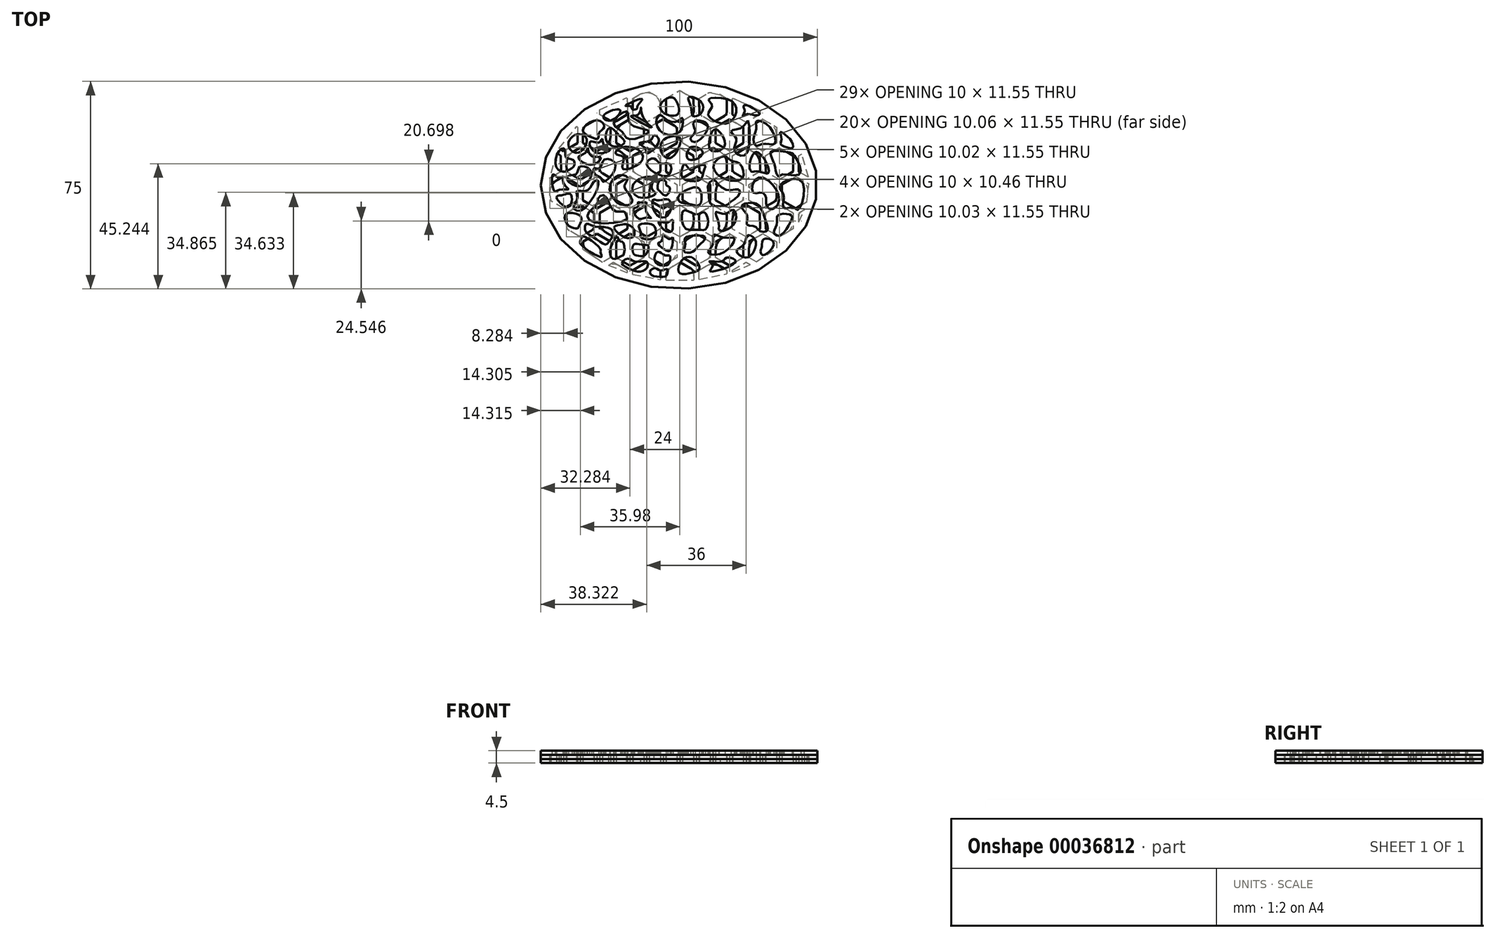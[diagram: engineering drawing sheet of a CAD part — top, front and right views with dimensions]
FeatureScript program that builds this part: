
annotation { "Feature Type Name" : "Feature", "Feature Type Description" : "" }
export const myFeature = defineFeature(function(context is Context, id is Id, definition is map)
    precondition{}
    {
        {
            var Q0;
            Q0=qCreatedBy(makeId("Top.planeOp"),FACE);
            var sketch = newSketch(context, id + "F0", { "sketchPlane" : qUnion([Q0])});
            skEllipse(sketch, "E0", {"center": v(0, 0) * mm, "majorRadius": 37.5 * mm, "minorRadius": 50 * mm, "majorAxis": v(0, 1)});
            skCircle(sketch, "E1.cCircle", {"center": v(-71.7, 28.44) * mm, "radius": 5 * mm, "construction": true});
            skLineSegment(sketch, "E1.0", {"start": v(-66.66, 25.61) * mm, "end": v(-71.63, 22.67) * mm, "construction": true});
            skLineSegment(sketch, "E1.1", {"start": v(-71.63, 22.67) * mm, "end": v(-76.66, 25.5) * mm, "construction": true});
            skLineSegment(sketch, "E1.2", {"start": v(-76.66, 25.5) * mm, "end": v(-76.73, 31.27) * mm, "construction": true});
            skLineSegment(sketch, "E1.3", {"start": v(-76.73, 31.27) * mm, "end": v(-71.76, 34.22) * mm, "construction": true});
            skLineSegment(sketch, "E1.4", {"start": v(-71.76, 34.22) * mm, "end": v(-66.73, 31.39) * mm, "construction": true});
            skLineSegment(sketch, "E1.5", {"start": v(-66.73, 31.39) * mm, "end": v(-66.66, 25.61) * mm, "construction": true});
            skPoint(sketch, "E1.0.midPoint", {"position": v(-69.15, 24.14) * mm});
            skPoint(sketch, "E2", {"position": v(-77.72, 18.06) * mm});
            skLineSegment(sketch, "E3", {"start": v(-71.7, 28.44) * mm, "end": v(-74.15, 24.08) * mm, "construction": true});
            skLineSegment(sketch, "E4", {"start": v(-71.7, 28.44) * mm, "end": v(-71.63, 14.25) * mm, "construction": true});
            skCircle(sketch, "E5.cCircle", {"center": v(-77.72, 18.06) * mm, "radius": 5 * mm, "construction": true});
            skLineSegment(sketch, "E5.0", {"start": v(-77.72, 23.84) * mm, "end": v(-72.72, 20.95) * mm, "construction": true});
            skLineSegment(sketch, "E5.1", {"start": v(-72.72, 20.95) * mm, "end": v(-72.72, 15.18) * mm, "construction": true});
            skLineSegment(sketch, "E5.2", {"start": v(-72.72, 15.18) * mm, "end": v(-77.72, 12.29) * mm, "construction": true});
            skLineSegment(sketch, "E5.3", {"start": v(-77.72, 12.29) * mm, "end": v(-82.72, 15.18) * mm, "construction": true});
            skLineSegment(sketch, "E5.4", {"start": v(-82.72, 15.18) * mm, "end": v(-82.72, 20.95) * mm, "construction": true});
            skLineSegment(sketch, "E5.5", {"start": v(-82.72, 20.95) * mm, "end": v(-77.72, 23.84) * mm, "construction": true});
            skPoint(sketch, "E5.0.midPoint", {"position": v(-75.22, 22.4) * mm});
            skLineSegment(sketch, "E6.0.1.0", {"start": v(-76.73, 10.57) * mm, "end": v(-71.76, 13.52) * mm});
            skLineSegment(sketch, "E6.0.1.1", {"start": v(-71.76, 13.52) * mm, "end": v(-66.73, 10.69) * mm});
            skLineSegment(sketch, "E6.0.1.2", {"start": v(-66.73, 10.69) * mm, "end": v(-66.66, 4.91) * mm});
            skLineSegment(sketch, "E6.0.1.3", {"start": v(-66.66, 4.91) * mm, "end": v(-71.63, 1.97) * mm});
            skLineSegment(sketch, "E6.0.1.4", {"start": v(-71.63, 1.97) * mm, "end": v(-76.66, 4.8) * mm});
            skLineSegment(sketch, "E6.0.1.5", {"start": v(-76.66, 4.8) * mm, "end": v(-76.73, 10.57) * mm});
            skLineSegment(sketch, "E6.0.1.6", {"start": v(-82.72, 0.25) * mm, "end": v(-77.72, 3.14) * mm});
            skLineSegment(sketch, "E6.0.1.7", {"start": v(-77.72, 3.14) * mm, "end": v(-72.72, 0.25) * mm});
            skLineSegment(sketch, "E6.0.1.8", {"start": v(-72.72, 0.25) * mm, "end": v(-72.72, -5.52) * mm});
            skLineSegment(sketch, "E6.0.1.9", {"start": v(-72.72, -5.52) * mm, "end": v(-77.72, -8.4) * mm});
            skLineSegment(sketch, "E6.0.1.10", {"start": v(-77.72, -8.4) * mm, "end": v(-82.72, -5.52) * mm});
            skLineSegment(sketch, "E6.0.1.11", {"start": v(-82.72, -5.52) * mm, "end": v(-82.72, 0.25) * mm});
            skLineSegment(sketch, "E6.0.2.0", {"start": v(-76.73, -10.12) * mm, "end": v(-71.76, -7.18) * mm});
            skLineSegment(sketch, "E6.0.2.1", {"start": v(-71.76, -7.18) * mm, "end": v(-66.73, -10.01) * mm});
            skLineSegment(sketch, "E6.0.2.2", {"start": v(-66.73, -10.01) * mm, "end": v(-66.66, -15.78) * mm});
            skLineSegment(sketch, "E6.0.2.3", {"start": v(-66.66, -15.78) * mm, "end": v(-71.63, -18.73) * mm});
            skLineSegment(sketch, "E6.0.2.4", {"start": v(-71.63, -18.73) * mm, "end": v(-76.66, -15.9) * mm});
            skLineSegment(sketch, "E6.0.2.5", {"start": v(-76.66, -15.9) * mm, "end": v(-76.73, -10.12) * mm});
            skLineSegment(sketch, "E6.0.2.6", {"start": v(-82.72, -20.45) * mm, "end": v(-77.72, -17.56) * mm});
            skLineSegment(sketch, "E6.0.2.7", {"start": v(-77.72, -17.56) * mm, "end": v(-72.72, -20.45) * mm});
            skLineSegment(sketch, "E6.0.2.8", {"start": v(-72.72, -20.45) * mm, "end": v(-72.72, -26.22) * mm});
            skLineSegment(sketch, "E6.0.2.9", {"start": v(-72.72, -26.22) * mm, "end": v(-77.72, -29.1) * mm});
            skLineSegment(sketch, "E6.0.2.10", {"start": v(-77.72, -29.1) * mm, "end": v(-82.72, -26.22) * mm});
            skLineSegment(sketch, "E6.0.2.11", {"start": v(-82.72, -26.22) * mm, "end": v(-82.72, -20.45) * mm});
            skLineSegment(sketch, "E6.0.3.0", {"start": v(-76.73, -30.82) * mm, "end": v(-71.76, -27.88) * mm});
            skLineSegment(sketch, "E6.0.3.1", {"start": v(-71.76, -27.88) * mm, "end": v(-66.73, -30.7) * mm});
            skLineSegment(sketch, "E6.0.3.2", {"start": v(-66.73, -30.7) * mm, "end": v(-66.66, -36.48) * mm});
            skLineSegment(sketch, "E6.0.3.3", {"start": v(-66.66, -36.48) * mm, "end": v(-71.63, -39.42) * mm});
            skLineSegment(sketch, "E6.0.3.4", {"start": v(-71.63, -39.42) * mm, "end": v(-76.66, -36.6) * mm});
            skLineSegment(sketch, "E6.0.3.5", {"start": v(-76.66, -36.6) * mm, "end": v(-76.73, -30.82) * mm});
            skLineSegment(sketch, "E6.0.3.6", {"start": v(-82.72, -41.14) * mm, "end": v(-77.72, -38.26) * mm});
            skLineSegment(sketch, "E6.0.3.7", {"start": v(-77.72, -38.26) * mm, "end": v(-72.72, -41.14) * mm});
            skLineSegment(sketch, "E6.0.3.8", {"start": v(-72.72, -41.14) * mm, "end": v(-72.72, -46.92) * mm});
            skLineSegment(sketch, "E6.0.3.9", {"start": v(-72.72, -46.92) * mm, "end": v(-77.72, -49.8) * mm});
            skLineSegment(sketch, "E6.0.3.10", {"start": v(-77.72, -49.8) * mm, "end": v(-82.72, -46.92) * mm});
            skLineSegment(sketch, "E6.0.3.11", {"start": v(-82.72, -46.92) * mm, "end": v(-82.72, -41.14) * mm});
            skLineSegment(sketch, "E6.1.1.0", {"start": v(-64.73, 10.57) * mm, "end": v(-59.76, 13.52) * mm});
            skLineSegment(sketch, "E6.1.1.1", {"start": v(-59.76, 13.52) * mm, "end": v(-54.73, 10.69) * mm});
            skLineSegment(sketch, "E6.1.1.2", {"start": v(-54.73, 10.69) * mm, "end": v(-54.66, 4.91) * mm});
            skLineSegment(sketch, "E6.1.1.3", {"start": v(-54.66, 4.91) * mm, "end": v(-59.63, 1.97) * mm});
            skLineSegment(sketch, "E6.1.1.4", {"start": v(-59.63, 1.97) * mm, "end": v(-64.66, 4.8) * mm});
            skLineSegment(sketch, "E6.1.1.5", {"start": v(-64.66, 4.8) * mm, "end": v(-64.73, 10.57) * mm});
            skLineSegment(sketch, "E6.1.1.6", {"start": v(-70.72, 0.25) * mm, "end": v(-65.72, 3.14) * mm});
            skLineSegment(sketch, "E6.1.1.7", {"start": v(-65.72, 3.14) * mm, "end": v(-60.72, 0.25) * mm});
            skLineSegment(sketch, "E6.1.1.8", {"start": v(-60.72, 0.25) * mm, "end": v(-60.72, -5.52) * mm});
            skLineSegment(sketch, "E6.1.1.9", {"start": v(-60.72, -5.52) * mm, "end": v(-65.72, -8.4) * mm});
            skLineSegment(sketch, "E6.1.1.10", {"start": v(-65.72, -8.4) * mm, "end": v(-70.72, -5.52) * mm});
            skLineSegment(sketch, "E6.1.1.11", {"start": v(-70.72, -5.52) * mm, "end": v(-70.72, 0.25) * mm});
            skLineSegment(sketch, "E6.1.2.0", {"start": v(-64.73, -10.12) * mm, "end": v(-59.76, -7.18) * mm});
            skLineSegment(sketch, "E6.1.2.1", {"start": v(-59.76, -7.18) * mm, "end": v(-54.73, -10.01) * mm});
            skLineSegment(sketch, "E6.1.2.2", {"start": v(-54.73, -10.01) * mm, "end": v(-54.66, -15.78) * mm});
            skLineSegment(sketch, "E6.1.2.3", {"start": v(-54.66, -15.78) * mm, "end": v(-59.63, -18.73) * mm});
            skLineSegment(sketch, "E6.1.2.4", {"start": v(-59.63, -18.73) * mm, "end": v(-64.66, -15.9) * mm});
            skLineSegment(sketch, "E6.1.2.5", {"start": v(-64.66, -15.9) * mm, "end": v(-64.73, -10.12) * mm});
            skLineSegment(sketch, "E6.1.2.6", {"start": v(-70.72, -20.45) * mm, "end": v(-65.72, -17.56) * mm});
            skLineSegment(sketch, "E6.1.2.7", {"start": v(-65.72, -17.56) * mm, "end": v(-60.72, -20.45) * mm});
            skLineSegment(sketch, "E6.1.2.8", {"start": v(-60.72, -20.45) * mm, "end": v(-60.72, -26.22) * mm});
            skLineSegment(sketch, "E6.1.2.9", {"start": v(-60.72, -26.22) * mm, "end": v(-65.72, -29.1) * mm});
            skLineSegment(sketch, "E6.1.2.10", {"start": v(-65.72, -29.1) * mm, "end": v(-70.72, -26.22) * mm});
            skLineSegment(sketch, "E6.1.2.11", {"start": v(-70.72, -26.22) * mm, "end": v(-70.72, -20.45) * mm});
            skLineSegment(sketch, "E6.1.3.0", {"start": v(-64.73, -30.82) * mm, "end": v(-59.76, -27.88) * mm});
            skLineSegment(sketch, "E6.1.3.1", {"start": v(-59.76, -27.88) * mm, "end": v(-54.73, -30.7) * mm});
            skLineSegment(sketch, "E6.1.3.2", {"start": v(-54.73, -30.7) * mm, "end": v(-54.66, -36.48) * mm});
            skLineSegment(sketch, "E6.1.3.3", {"start": v(-54.66, -36.48) * mm, "end": v(-59.63, -39.42) * mm});
            skLineSegment(sketch, "E6.1.3.4", {"start": v(-59.63, -39.42) * mm, "end": v(-64.66, -36.6) * mm});
            skLineSegment(sketch, "E6.1.3.5", {"start": v(-64.66, -36.6) * mm, "end": v(-64.73, -30.82) * mm});
            skLineSegment(sketch, "E6.1.3.6", {"start": v(-70.72, -41.14) * mm, "end": v(-65.72, -38.26) * mm});
            skLineSegment(sketch, "E6.1.3.7", {"start": v(-65.72, -38.26) * mm, "end": v(-60.72, -41.14) * mm});
            skLineSegment(sketch, "E6.1.3.8", {"start": v(-60.72, -41.14) * mm, "end": v(-60.72, -46.92) * mm});
            skLineSegment(sketch, "E6.1.3.9", {"start": v(-60.72, -46.92) * mm, "end": v(-65.72, -49.8) * mm});
            skLineSegment(sketch, "E6.1.3.10", {"start": v(-65.72, -49.8) * mm, "end": v(-70.72, -46.92) * mm});
            skLineSegment(sketch, "E6.1.3.11", {"start": v(-70.72, -46.92) * mm, "end": v(-70.72, -41.14) * mm});
            skLineSegment(sketch, "E6.2.1.2", {"start": v(-42.73, 10.69) * mm, "end": v(-42.66, 4.91) * mm});
            skLineSegment(sketch, "E6.2.1.3", {"start": v(-42.66, 4.91) * mm, "end": v(-46.88, 2.41) * mm});
            skLineSegment(sketch, "E6.2.2.6", {"start": v(-58.72, -20.45) * mm, "end": v(-53.72, -17.56) * mm});
            skLineSegment(sketch, "E6.2.2.7", {"start": v(-53.72, -17.56) * mm, "end": v(-48.72, -20.45) * mm});
            skLineSegment(sketch, "E6.2.2.8", {"start": v(-48.72, -20.45) * mm, "end": v(-48.72, -26.22) * mm});
            skLineSegment(sketch, "E6.2.2.9", {"start": v(-48.72, -26.22) * mm, "end": v(-53.72, -29.1) * mm});
            skLineSegment(sketch, "E6.2.2.10", {"start": v(-53.72, -29.1) * mm, "end": v(-58.72, -26.22) * mm});
            skLineSegment(sketch, "E6.2.2.11", {"start": v(-58.72, -26.22) * mm, "end": v(-58.72, -20.45) * mm});
            skLineSegment(sketch, "E6.2.3.0", {"start": v(-52.73, -30.82) * mm, "end": v(-47.76, -27.88) * mm});
            skLineSegment(sketch, "E6.2.3.1", {"start": v(-47.76, -27.88) * mm, "end": v(-42.73, -30.7) * mm});
            skLineSegment(sketch, "E6.2.3.2", {"start": v(-42.73, -30.7) * mm, "end": v(-42.66, -36.48) * mm});
            skLineSegment(sketch, "E6.2.3.3", {"start": v(-42.66, -36.48) * mm, "end": v(-47.63, -39.42) * mm});
            skLineSegment(sketch, "E6.2.3.4", {"start": v(-47.63, -39.42) * mm, "end": v(-52.66, -36.6) * mm});
            skLineSegment(sketch, "E6.2.3.5", {"start": v(-52.66, -36.6) * mm, "end": v(-52.73, -30.82) * mm});
            skLineSegment(sketch, "E6.2.3.6", {"start": v(-58.72, -41.14) * mm, "end": v(-53.72, -38.26) * mm});
            skLineSegment(sketch, "E6.2.3.7", {"start": v(-53.72, -38.26) * mm, "end": v(-48.72, -41.14) * mm});
            skLineSegment(sketch, "E6.2.3.8", {"start": v(-48.72, -41.14) * mm, "end": v(-48.72, -46.92) * mm});
            skLineSegment(sketch, "E6.2.3.9", {"start": v(-48.72, -46.92) * mm, "end": v(-53.72, -49.8) * mm});
            skLineSegment(sketch, "E6.2.3.10", {"start": v(-53.72, -49.8) * mm, "end": v(-58.72, -46.92) * mm});
            skLineSegment(sketch, "E6.2.3.11", {"start": v(-58.72, -46.92) * mm, "end": v(-58.72, -41.14) * mm});
            skLineSegment(sketch, "E6.3.0.8", {"start": v(-36.72, 20.95) * mm, "end": v(-36.72, 15.18) * mm});
            skLineSegment(sketch, "E6.3.0.9", {"start": v(-36.72, 15.18) * mm, "end": v(-41.72, 12.29) * mm});
            skLineSegment(sketch, "E6.3.0.10", {"start": v(-41.72, 12.29) * mm, "end": v(-43.37, 13.25) * mm});
            skLineSegment(sketch, "E6.3.1.0", {"start": v(-40.73, 10.57) * mm, "end": v(-35.76, 13.52) * mm});
            skLineSegment(sketch, "E6.3.1.1", {"start": v(-35.76, 13.52) * mm, "end": v(-30.73, 10.69) * mm});
            skLineSegment(sketch, "E6.3.1.2", {"start": v(-30.73, 10.69) * mm, "end": v(-30.66, 4.91) * mm});
            skLineSegment(sketch, "E6.3.1.3", {"start": v(-30.66, 4.91) * mm, "end": v(-35.63, 1.97) * mm});
            skLineSegment(sketch, "E6.3.1.4", {"start": v(-35.63, 1.97) * mm, "end": v(-40.66, 4.8) * mm});
            skLineSegment(sketch, "E6.3.1.5", {"start": v(-40.66, 4.8) * mm, "end": v(-40.73, 10.57) * mm});
            skLineSegment(sketch, "E6.3.1.6", {"start": v(-46.72, 0.25) * mm, "end": v(-41.72, 3.14) * mm});
            skLineSegment(sketch, "E6.3.1.7", {"start": v(-41.72, 3.14) * mm, "end": v(-36.72, 0.25) * mm});
            skLineSegment(sketch, "E6.3.1.8", {"start": v(-36.72, 0.25) * mm, "end": v(-36.72, -5.52) * mm});
            skLineSegment(sketch, "E6.3.1.9", {"start": v(-36.72, -5.52) * mm, "end": v(-41.72, -8.4) * mm});
            skLineSegment(sketch, "E6.3.1.10", {"start": v(-41.72, -8.4) * mm, "end": v(-46.34, -5.74) * mm});
            skLineSegment(sketch, "E6.3.1.11", {"start": v(-46.72, -3.77) * mm, "end": v(-46.72, 0.25) * mm});
            skLineSegment(sketch, "E6.3.2.0", {"start": v(-40.73, -10.12) * mm, "end": v(-35.76, -7.18) * mm});
            skLineSegment(sketch, "E6.3.2.1", {"start": v(-35.76, -7.18) * mm, "end": v(-30.73, -10.01) * mm});
            skLineSegment(sketch, "E6.3.2.2", {"start": v(-30.73, -10.01) * mm, "end": v(-30.66, -15.78) * mm});
            skLineSegment(sketch, "E6.3.2.3", {"start": v(-30.66, -15.78) * mm, "end": v(-35.63, -18.73) * mm});
            skLineSegment(sketch, "E6.3.2.4", {"start": v(-35.63, -18.73) * mm, "end": v(-40.66, -15.9) * mm});
            skLineSegment(sketch, "E6.3.2.5", {"start": v(-40.66, -15.9) * mm, "end": v(-40.73, -10.12) * mm});
            skLineSegment(sketch, "E6.3.3.0", {"start": v(-40.73, -30.82) * mm, "end": v(-35.76, -27.88) * mm});
            skLineSegment(sketch, "E6.3.3.1", {"start": v(-35.76, -27.88) * mm, "end": v(-30.73, -30.7) * mm});
            skLineSegment(sketch, "E6.3.3.2", {"start": v(-30.73, -30.7) * mm, "end": v(-30.66, -36.48) * mm});
            skLineSegment(sketch, "E6.3.3.3", {"start": v(-30.66, -36.48) * mm, "end": v(-35.63, -39.42) * mm});
            skLineSegment(sketch, "E6.3.3.4", {"start": v(-35.63, -39.42) * mm, "end": v(-40.66, -36.6) * mm});
            skLineSegment(sketch, "E6.3.3.5", {"start": v(-40.66, -36.6) * mm, "end": v(-40.73, -30.82) * mm});
            skLineSegment(sketch, "E6.3.3.6", {"start": v(-46.72, -41.14) * mm, "end": v(-41.72, -38.26) * mm});
            skLineSegment(sketch, "E6.3.3.7", {"start": v(-41.72, -38.26) * mm, "end": v(-36.72, -41.14) * mm});
            skLineSegment(sketch, "E6.3.3.8", {"start": v(-36.72, -41.14) * mm, "end": v(-36.72, -46.92) * mm});
            skLineSegment(sketch, "E6.3.3.9", {"start": v(-36.72, -46.92) * mm, "end": v(-41.72, -49.8) * mm});
            skLineSegment(sketch, "E6.3.3.10", {"start": v(-41.72, -49.8) * mm, "end": v(-46.72, -46.92) * mm});
            skLineSegment(sketch, "E6.3.3.11", {"start": v(-46.72, -46.92) * mm, "end": v(-46.72, -41.14) * mm});
            skLineSegment(sketch, "E6.4.0.2", {"start": v(-18.73, 31.39) * mm, "end": v(-18.66, 25.61) * mm});
            skLineSegment(sketch, "E6.4.0.3", {"start": v(-18.66, 25.61) * mm, "end": v(-23.63, 22.67) * mm});
            skLineSegment(sketch, "E6.4.0.4", {"start": v(-23.63, 22.67) * mm, "end": v(-28.66, 25.5) * mm});
            skLineSegment(sketch, "E6.4.0.5", {"start": v(-28.66, 25.5) * mm, "end": v(-28.68, 27.3) * mm});
            skLineSegment(sketch, "E6.4.0.6", {"start": v(-34.72, 20.95) * mm, "end": v(-29.72, 23.84) * mm});
            skLineSegment(sketch, "E6.4.0.7", {"start": v(-29.72, 23.84) * mm, "end": v(-24.72, 20.95) * mm});
            skLineSegment(sketch, "E6.4.0.8", {"start": v(-24.72, 20.95) * mm, "end": v(-24.72, 15.18) * mm});
            skLineSegment(sketch, "E6.4.0.9", {"start": v(-24.72, 15.18) * mm, "end": v(-29.72, 12.29) * mm});
            skLineSegment(sketch, "E6.4.0.10", {"start": v(-29.72, 12.29) * mm, "end": v(-34.72, 15.18) * mm});
            skLineSegment(sketch, "E6.4.0.11", {"start": v(-34.72, 15.18) * mm, "end": v(-34.72, 20.95) * mm});
            skLineSegment(sketch, "E6.4.1.0", {"start": v(-28.73, 10.57) * mm, "end": v(-23.76, 13.52) * mm});
            skLineSegment(sketch, "E6.4.1.1", {"start": v(-23.76, 13.52) * mm, "end": v(-18.73, 10.69) * mm});
            skLineSegment(sketch, "E6.4.1.2", {"start": v(-18.73, 10.69) * mm, "end": v(-18.66, 4.91) * mm});
            skLineSegment(sketch, "E6.4.1.3", {"start": v(-18.66, 4.91) * mm, "end": v(-23.63, 1.97) * mm});
            skLineSegment(sketch, "E6.4.1.4", {"start": v(-23.63, 1.97) * mm, "end": v(-28.66, 4.8) * mm});
            skLineSegment(sketch, "E6.4.1.5", {"start": v(-28.66, 4.8) * mm, "end": v(-28.73, 10.57) * mm});
            skLineSegment(sketch, "E6.4.1.6", {"start": v(-34.72, 0.25) * mm, "end": v(-29.72, 3.14) * mm});
            skLineSegment(sketch, "E6.4.1.7", {"start": v(-29.72, 3.14) * mm, "end": v(-24.72, 0.25) * mm});
            skLineSegment(sketch, "E6.4.1.8", {"start": v(-24.72, 0.25) * mm, "end": v(-24.72, -5.52) * mm});
            skLineSegment(sketch, "E6.4.1.9", {"start": v(-24.72, -5.52) * mm, "end": v(-29.72, -8.4) * mm});
            skLineSegment(sketch, "E6.4.1.10", {"start": v(-29.72, -8.4) * mm, "end": v(-34.72, -5.52) * mm});
            skLineSegment(sketch, "E6.4.1.11", {"start": v(-34.72, -5.52) * mm, "end": v(-34.72, 0.25) * mm});
            skLineSegment(sketch, "E6.4.2.0", {"start": v(-28.73, -10.12) * mm, "end": v(-23.76, -7.18) * mm});
            skLineSegment(sketch, "E6.4.2.1", {"start": v(-23.76, -7.18) * mm, "end": v(-18.73, -10.01) * mm});
            skLineSegment(sketch, "E6.4.2.2", {"start": v(-18.73, -10.01) * mm, "end": v(-18.66, -15.78) * mm});
            skLineSegment(sketch, "E6.4.2.3", {"start": v(-18.66, -15.78) * mm, "end": v(-23.63, -18.73) * mm});
            skLineSegment(sketch, "E6.4.2.4", {"start": v(-23.63, -18.73) * mm, "end": v(-28.66, -15.9) * mm});
            skLineSegment(sketch, "E6.4.2.5", {"start": v(-28.66, -15.9) * mm, "end": v(-28.73, -10.12) * mm});
            skLineSegment(sketch, "E6.4.2.6", {"start": v(-34.72, -20.45) * mm, "end": v(-29.72, -17.56) * mm});
            skLineSegment(sketch, "E6.4.2.7", {"start": v(-29.72, -17.56) * mm, "end": v(-24.72, -20.45) * mm});
            skLineSegment(sketch, "E6.4.2.8", {"start": v(-24.72, -20.45) * mm, "end": v(-24.72, -26.22) * mm});
            skLineSegment(sketch, "E6.4.2.9", {"start": v(-24.72, -26.22) * mm, "end": v(-27.6, -27.89) * mm});
            skLineSegment(sketch, "E6.4.2.11", {"start": v(-34.72, -23.21) * mm, "end": v(-34.72, -20.45) * mm});
            skLineSegment(sketch, "E6.4.3.1", {"start": v(-23.76, -27.88) * mm, "end": v(-18.73, -30.7) * mm});
            skLineSegment(sketch, "E6.4.3.2", {"start": v(-18.73, -30.7) * mm, "end": v(-18.72, -31.63) * mm});
            skLineSegment(sketch, "E6.4.3.6", {"start": v(-34.72, -41.14) * mm, "end": v(-29.72, -38.26) * mm});
            skLineSegment(sketch, "E6.4.3.7", {"start": v(-29.72, -38.26) * mm, "end": v(-24.72, -41.14) * mm});
            skLineSegment(sketch, "E6.4.3.8", {"start": v(-24.72, -41.14) * mm, "end": v(-24.72, -46.92) * mm});
            skLineSegment(sketch, "E6.4.3.9", {"start": v(-24.72, -46.92) * mm, "end": v(-29.72, -49.8) * mm});
            skLineSegment(sketch, "E6.4.3.10", {"start": v(-29.72, -49.8) * mm, "end": v(-34.72, -46.92) * mm});
            skLineSegment(sketch, "E6.4.3.11", {"start": v(-34.72, -46.92) * mm, "end": v(-34.72, -41.14) * mm});
            skLineSegment(sketch, "E6.5.0.0", {"start": v(-16.73, 31.27) * mm, "end": v(-13.9, 32.95) * mm});
            skLineSegment(sketch, "E6.5.0.1", {"start": v(-10.66, 33.6) * mm, "end": v(-6.73, 31.39) * mm});
            skLineSegment(sketch, "E6.5.0.2", {"start": v(-6.73, 31.39) * mm, "end": v(-6.66, 25.61) * mm});
            skLineSegment(sketch, "E6.5.0.3", {"start": v(-6.66, 25.61) * mm, "end": v(-11.63, 22.67) * mm});
            skLineSegment(sketch, "E6.5.0.4", {"start": v(-11.63, 22.67) * mm, "end": v(-16.66, 25.5) * mm});
            skLineSegment(sketch, "E6.5.0.5", {"start": v(-16.66, 25.5) * mm, "end": v(-16.73, 31.27) * mm});
            skLineSegment(sketch, "E6.5.0.6", {"start": v(-22.72, 20.95) * mm, "end": v(-17.72, 23.84) * mm});
            skLineSegment(sketch, "E6.5.0.7", {"start": v(-17.72, 23.84) * mm, "end": v(-12.72, 20.95) * mm});
            skLineSegment(sketch, "E6.5.0.8", {"start": v(-12.72, 20.95) * mm, "end": v(-12.72, 15.18) * mm});
            skLineSegment(sketch, "E6.5.0.9", {"start": v(-12.72, 15.18) * mm, "end": v(-17.72, 12.29) * mm});
            skLineSegment(sketch, "E6.5.0.10", {"start": v(-17.72, 12.29) * mm, "end": v(-22.72, 15.18) * mm});
            skLineSegment(sketch, "E6.5.0.11", {"start": v(-22.72, 15.18) * mm, "end": v(-22.72, 20.95) * mm});
            skLineSegment(sketch, "E6.5.1.0", {"start": v(-16.73, 10.57) * mm, "end": v(-11.76, 13.52) * mm});
            skLineSegment(sketch, "E6.5.1.1", {"start": v(-11.76, 13.52) * mm, "end": v(-6.73, 10.69) * mm});
            skLineSegment(sketch, "E6.5.1.2", {"start": v(-6.73, 10.69) * mm, "end": v(-6.66, 4.91) * mm});
            skLineSegment(sketch, "E6.5.1.3", {"start": v(-6.66, 4.91) * mm, "end": v(-11.63, 1.97) * mm});
            skLineSegment(sketch, "E6.5.1.4", {"start": v(-11.63, 1.97) * mm, "end": v(-16.66, 4.8) * mm});
            skLineSegment(sketch, "E6.5.1.5", {"start": v(-16.66, 4.8) * mm, "end": v(-16.73, 10.57) * mm});
            skLineSegment(sketch, "E6.5.1.6", {"start": v(-22.72, 0.25) * mm, "end": v(-17.72, 3.14) * mm});
            skLineSegment(sketch, "E6.5.1.7", {"start": v(-17.72, 3.14) * mm, "end": v(-12.72, 0.25) * mm});
            skLineSegment(sketch, "E6.5.1.8", {"start": v(-12.72, 0.25) * mm, "end": v(-12.72, -5.52) * mm});
            skLineSegment(sketch, "E6.5.1.9", {"start": v(-12.72, -5.52) * mm, "end": v(-17.72, -8.4) * mm});
            skLineSegment(sketch, "E6.5.1.10", {"start": v(-17.72, -8.4) * mm, "end": v(-22.72, -5.52) * mm});
            skLineSegment(sketch, "E6.5.1.11", {"start": v(-22.72, -5.52) * mm, "end": v(-22.72, 0.25) * mm});
            skLineSegment(sketch, "E6.5.2.0", {"start": v(-16.73, -10.12) * mm, "end": v(-11.76, -7.18) * mm});
            skLineSegment(sketch, "E6.5.2.1", {"start": v(-11.76, -7.18) * mm, "end": v(-6.73, -10.01) * mm});
            skLineSegment(sketch, "E6.5.2.2", {"start": v(-6.73, -10.01) * mm, "end": v(-6.66, -15.78) * mm});
            skLineSegment(sketch, "E6.5.2.3", {"start": v(-6.66, -15.78) * mm, "end": v(-11.63, -18.73) * mm});
            skLineSegment(sketch, "E6.5.2.4", {"start": v(-11.63, -18.73) * mm, "end": v(-16.66, -15.9) * mm});
            skLineSegment(sketch, "E6.5.2.5", {"start": v(-16.66, -15.9) * mm, "end": v(-16.73, -10.12) * mm});
            skLineSegment(sketch, "E6.5.2.6", {"start": v(-22.72, -20.45) * mm, "end": v(-17.72, -17.56) * mm});
            skLineSegment(sketch, "E6.5.2.7", {"start": v(-17.72, -17.56) * mm, "end": v(-12.72, -20.45) * mm});
            skLineSegment(sketch, "E6.5.2.8", {"start": v(-12.72, -20.45) * mm, "end": v(-12.72, -26.22) * mm});
            skLineSegment(sketch, "E6.5.2.9", {"start": v(-12.72, -26.22) * mm, "end": v(-17.72, -29.1) * mm});
            skLineSegment(sketch, "E6.5.2.10", {"start": v(-17.72, -29.1) * mm, "end": v(-22.72, -26.22) * mm});
            skLineSegment(sketch, "E6.5.2.11", {"start": v(-22.72, -26.22) * mm, "end": v(-22.72, -20.45) * mm});
            skLineSegment(sketch, "E6.5.3.0", {"start": v(-16.73, -30.82) * mm, "end": v(-11.76, -27.88) * mm});
            skLineSegment(sketch, "E6.5.3.1", {"start": v(-11.76, -27.88) * mm, "end": v(-6.73, -30.7) * mm});
            skLineSegment(sketch, "E6.5.3.2", {"start": v(-6.73, -30.7) * mm, "end": v(-6.69, -34.15) * mm});
            skLineSegment(sketch, "E6.5.3.6", {"start": v(-22.72, -41.14) * mm, "end": v(-17.72, -38.26) * mm});
            skLineSegment(sketch, "E6.5.3.7", {"start": v(-17.72, -38.26) * mm, "end": v(-12.72, -41.14) * mm});
            skLineSegment(sketch, "E6.5.3.8", {"start": v(-12.72, -41.14) * mm, "end": v(-12.72, -46.92) * mm});
            skLineSegment(sketch, "E6.5.3.9", {"start": v(-12.72, -46.92) * mm, "end": v(-17.72, -49.8) * mm});
            skLineSegment(sketch, "E6.5.3.10", {"start": v(-17.72, -49.8) * mm, "end": v(-22.72, -46.92) * mm});
            skLineSegment(sketch, "E6.5.3.11", {"start": v(-22.72, -46.92) * mm, "end": v(-22.72, -41.14) * mm});
            skLineSegment(sketch, "E6.6.0.0", {"start": v(-4.73, 31.27) * mm, "end": v(0.24, 34.22) * mm});
            skLineSegment(sketch, "E6.6.0.1", {"start": v(0.24, 34.22) * mm, "end": v(5.27, 31.39) * mm});
            skLineSegment(sketch, "E6.6.0.2", {"start": v(5.27, 31.39) * mm, "end": v(5.34, 25.61) * mm});
            skLineSegment(sketch, "E6.6.0.3", {"start": v(5.34, 25.61) * mm, "end": v(0.37, 22.67) * mm});
            skLineSegment(sketch, "E6.6.0.4", {"start": v(0.37, 22.67) * mm, "end": v(-4.66, 25.5) * mm});
            skLineSegment(sketch, "E6.6.0.5", {"start": v(-4.66, 25.5) * mm, "end": v(-4.73, 31.27) * mm});
            skLineSegment(sketch, "E6.6.0.6", {"start": v(-10.72, 20.95) * mm, "end": v(-5.72, 23.84) * mm});
            skLineSegment(sketch, "E6.6.0.7", {"start": v(-5.72, 23.84) * mm, "end": v(-0.72, 20.95) * mm});
            skLineSegment(sketch, "E6.6.0.8", {"start": v(-0.72, 20.95) * mm, "end": v(-0.72, 15.18) * mm});
            skLineSegment(sketch, "E6.6.0.9", {"start": v(-0.72, 15.18) * mm, "end": v(-5.72, 12.29) * mm});
            skLineSegment(sketch, "E6.6.0.10", {"start": v(-5.72, 12.29) * mm, "end": v(-10.72, 15.18) * mm});
            skLineSegment(sketch, "E6.6.0.11", {"start": v(-10.72, 15.18) * mm, "end": v(-10.72, 20.95) * mm});
            skLineSegment(sketch, "E6.6.1.0", {"start": v(-4.73, 10.57) * mm, "end": v(0.24, 13.52) * mm});
            skLineSegment(sketch, "E6.6.1.1", {"start": v(0.24, 13.52) * mm, "end": v(5.27, 10.69) * mm});
            skLineSegment(sketch, "E6.6.1.2", {"start": v(5.27, 10.69) * mm, "end": v(5.34, 4.91) * mm});
            skLineSegment(sketch, "E6.6.1.3", {"start": v(5.34, 4.91) * mm, "end": v(0.37, 1.97) * mm});
            skLineSegment(sketch, "E6.6.1.4", {"start": v(0.37, 1.97) * mm, "end": v(-4.66, 4.8) * mm});
            skLineSegment(sketch, "E6.6.1.5", {"start": v(-4.66, 4.8) * mm, "end": v(-4.73, 10.57) * mm});
            skLineSegment(sketch, "E6.6.1.6", {"start": v(-10.72, 0.25) * mm, "end": v(-5.72, 3.14) * mm});
            skLineSegment(sketch, "E6.6.1.7", {"start": v(-5.72, 3.14) * mm, "end": v(-0.72, 0.25) * mm});
            skLineSegment(sketch, "E6.6.1.8", {"start": v(-0.72, 0.25) * mm, "end": v(-0.72, -5.52) * mm});
            skLineSegment(sketch, "E6.6.1.9", {"start": v(-0.72, -5.52) * mm, "end": v(-5.72, -8.4) * mm});
            skLineSegment(sketch, "E6.6.1.10", {"start": v(-5.72, -8.4) * mm, "end": v(-10.72, -5.52) * mm});
            skLineSegment(sketch, "E6.6.1.11", {"start": v(-10.72, -5.52) * mm, "end": v(-10.72, 0.25) * mm});
            skLineSegment(sketch, "E6.6.2.0", {"start": v(-4.73, -10.12) * mm, "end": v(0.24, -7.18) * mm});
            skLineSegment(sketch, "E6.6.2.1", {"start": v(0.24, -7.18) * mm, "end": v(5.27, -10.01) * mm});
            skLineSegment(sketch, "E6.6.2.2", {"start": v(5.27, -10.01) * mm, "end": v(5.34, -15.78) * mm});
            skLineSegment(sketch, "E6.6.2.3", {"start": v(5.34, -15.78) * mm, "end": v(0.37, -18.73) * mm});
            skLineSegment(sketch, "E6.6.2.4", {"start": v(0.37, -18.73) * mm, "end": v(-4.66, -15.9) * mm});
            skLineSegment(sketch, "E6.6.2.5", {"start": v(-4.66, -15.9) * mm, "end": v(-4.73, -10.12) * mm});
            skLineSegment(sketch, "E6.6.2.6", {"start": v(-10.72, -20.45) * mm, "end": v(-5.72, -17.56) * mm});
            skLineSegment(sketch, "E6.6.2.7", {"start": v(-5.72, -17.56) * mm, "end": v(-0.72, -20.45) * mm});
            skLineSegment(sketch, "E6.6.2.8", {"start": v(-0.72, -20.45) * mm, "end": v(-0.72, -26.22) * mm});
            skLineSegment(sketch, "E6.6.2.9", {"start": v(-0.72, -26.22) * mm, "end": v(-5.72, -29.1) * mm});
            skLineSegment(sketch, "E6.6.2.10", {"start": v(-5.72, -29.1) * mm, "end": v(-10.72, -26.22) * mm});
            skLineSegment(sketch, "E6.6.2.11", {"start": v(-10.72, -26.22) * mm, "end": v(-10.72, -20.45) * mm});
            skLineSegment(sketch, "E6.6.3.0", {"start": v(-4.73, -30.82) * mm, "end": v(0.24, -27.88) * mm});
            skLineSegment(sketch, "E6.6.3.1", {"start": v(0.24, -27.88) * mm, "end": v(5.27, -30.7) * mm});
            skLineSegment(sketch, "E6.6.3.2", {"start": v(5.27, -30.7) * mm, "end": v(5.31, -34.28) * mm});
            skLineSegment(sketch, "E6.6.3.5", {"start": v(-4.69, -34.33) * mm, "end": v(-4.73, -30.82) * mm});
            skLineSegment(sketch, "E6.6.3.6", {"start": v(-10.72, -41.14) * mm, "end": v(-5.72, -38.26) * mm});
            skLineSegment(sketch, "E6.6.3.7", {"start": v(-5.72, -38.26) * mm, "end": v(-0.72, -41.14) * mm});
            skLineSegment(sketch, "E6.6.3.8", {"start": v(-0.72, -41.14) * mm, "end": v(-0.72, -46.92) * mm});
            skLineSegment(sketch, "E6.6.3.9", {"start": v(-0.72, -46.92) * mm, "end": v(-5.72, -49.8) * mm});
            skLineSegment(sketch, "E6.6.3.10", {"start": v(-5.72, -49.8) * mm, "end": v(-10.72, -46.92) * mm});
            skLineSegment(sketch, "E6.6.3.11", {"start": v(-10.72, -46.92) * mm, "end": v(-10.72, -41.14) * mm});
            skLineSegment(sketch, "E6.7.0.0", {"start": v(7.27, 31.27) * mm, "end": v(11.07, 33.52) * mm});
            skLineSegment(sketch, "E6.7.0.1", {"start": v(14.93, 32.7) * mm, "end": v(17.27, 31.39) * mm});
            skLineSegment(sketch, "E6.7.0.2", {"start": v(17.27, 31.39) * mm, "end": v(17.34, 25.61) * mm});
            skLineSegment(sketch, "E6.7.0.3", {"start": v(17.34, 25.61) * mm, "end": v(12.37, 22.67) * mm});
            skLineSegment(sketch, "E6.7.0.4", {"start": v(12.37, 22.67) * mm, "end": v(7.34, 25.5) * mm});
            skLineSegment(sketch, "E6.7.0.5", {"start": v(7.34, 25.5) * mm, "end": v(7.27, 31.27) * mm});
            skLineSegment(sketch, "E6.7.0.6", {"start": v(1.28, 20.95) * mm, "end": v(6.28, 23.84) * mm});
            skLineSegment(sketch, "E6.7.0.7", {"start": v(6.28, 23.84) * mm, "end": v(11.28, 20.95) * mm});
            skLineSegment(sketch, "E6.7.0.8", {"start": v(11.28, 20.95) * mm, "end": v(11.28, 15.18) * mm});
            skLineSegment(sketch, "E6.7.0.9", {"start": v(11.28, 15.18) * mm, "end": v(6.28, 12.29) * mm});
            skLineSegment(sketch, "E6.7.0.10", {"start": v(6.28, 12.29) * mm, "end": v(1.28, 15.18) * mm});
            skLineSegment(sketch, "E6.7.0.11", {"start": v(1.28, 15.18) * mm, "end": v(1.28, 20.95) * mm});
            skLineSegment(sketch, "E6.7.1.0", {"start": v(7.27, 10.57) * mm, "end": v(12.24, 13.52) * mm});
            skLineSegment(sketch, "E6.7.1.1", {"start": v(12.24, 13.52) * mm, "end": v(17.27, 10.69) * mm});
            skLineSegment(sketch, "E6.7.1.2", {"start": v(17.27, 10.69) * mm, "end": v(17.34, 4.91) * mm});
            skLineSegment(sketch, "E6.7.1.3", {"start": v(17.34, 4.91) * mm, "end": v(12.37, 1.97) * mm});
            skLineSegment(sketch, "E6.7.1.4", {"start": v(12.37, 1.97) * mm, "end": v(7.34, 4.8) * mm});
            skLineSegment(sketch, "E6.7.1.5", {"start": v(7.34, 4.8) * mm, "end": v(7.27, 10.57) * mm});
            skLineSegment(sketch, "E6.7.1.6", {"start": v(1.28, 0.25) * mm, "end": v(6.28, 3.14) * mm});
            skLineSegment(sketch, "E6.7.1.7", {"start": v(6.28, 3.14) * mm, "end": v(11.28, 0.25) * mm});
            skLineSegment(sketch, "E6.7.1.8", {"start": v(11.28, 0.25) * mm, "end": v(11.28, -5.52) * mm});
            skLineSegment(sketch, "E6.7.1.9", {"start": v(11.28, -5.52) * mm, "end": v(6.28, -8.4) * mm});
            skLineSegment(sketch, "E6.7.1.10", {"start": v(6.28, -8.4) * mm, "end": v(1.28, -5.52) * mm});
            skLineSegment(sketch, "E6.7.1.11", {"start": v(1.28, -5.52) * mm, "end": v(1.28, 0.25) * mm});
            skLineSegment(sketch, "E6.7.2.0", {"start": v(7.27, -10.12) * mm, "end": v(12.24, -7.18) * mm});
            skLineSegment(sketch, "E6.7.2.1", {"start": v(12.24, -7.18) * mm, "end": v(17.27, -10.01) * mm});
            skLineSegment(sketch, "E6.7.2.2", {"start": v(17.27, -10.01) * mm, "end": v(17.34, -15.78) * mm});
            skLineSegment(sketch, "E6.7.2.3", {"start": v(17.34, -15.78) * mm, "end": v(12.37, -18.73) * mm});
            skLineSegment(sketch, "E6.7.2.4", {"start": v(12.37, -18.73) * mm, "end": v(7.34, -15.9) * mm});
            skLineSegment(sketch, "E6.7.2.5", {"start": v(7.34, -15.9) * mm, "end": v(7.27, -10.12) * mm});
            skLineSegment(sketch, "E6.7.2.6", {"start": v(1.28, -20.45) * mm, "end": v(6.28, -17.56) * mm});
            skLineSegment(sketch, "E6.7.2.7", {"start": v(6.28, -17.56) * mm, "end": v(11.28, -20.45) * mm});
            skLineSegment(sketch, "E6.7.2.8", {"start": v(11.28, -20.45) * mm, "end": v(11.28, -26.22) * mm});
            skLineSegment(sketch, "E6.7.2.9", {"start": v(11.28, -26.22) * mm, "end": v(6.28, -29.1) * mm});
            skLineSegment(sketch, "E6.7.2.10", {"start": v(6.28, -29.1) * mm, "end": v(1.28, -26.22) * mm});
            skLineSegment(sketch, "E6.7.2.11", {"start": v(1.28, -26.22) * mm, "end": v(1.28, -20.45) * mm});
            skLineSegment(sketch, "E6.7.3.0", {"start": v(7.27, -30.82) * mm, "end": v(12.24, -27.88) * mm});
            skLineSegment(sketch, "E6.7.3.1", {"start": v(12.24, -27.88) * mm, "end": v(17.27, -30.7) * mm});
            skLineSegment(sketch, "E6.7.3.2", {"start": v(17.27, -30.7) * mm, "end": v(17.29, -32.07) * mm});
            skLineSegment(sketch, "E6.7.3.5", {"start": v(7.3, -34.08) * mm, "end": v(7.27, -30.82) * mm});
            skLineSegment(sketch, "E6.7.3.6", {"start": v(1.28, -41.14) * mm, "end": v(6.28, -38.26) * mm});
            skLineSegment(sketch, "E6.7.3.7", {"start": v(6.28, -38.26) * mm, "end": v(11.28, -41.14) * mm});
            skLineSegment(sketch, "E6.7.3.8", {"start": v(11.28, -41.14) * mm, "end": v(11.28, -46.92) * mm});
            skLineSegment(sketch, "E6.7.3.9", {"start": v(11.28, -46.92) * mm, "end": v(6.28, -49.8) * mm});
            skLineSegment(sketch, "E6.7.3.10", {"start": v(6.28, -49.8) * mm, "end": v(1.28, -46.92) * mm});
            skLineSegment(sketch, "E6.7.3.11", {"start": v(1.28, -46.92) * mm, "end": v(1.28, -41.14) * mm});
            skLineSegment(sketch, "E6.8.0.0", {"start": v(19.27, 31.27) * mm, "end": v(19.47, 31.39) * mm});
            skLineSegment(sketch, "E6.8.0.2", {"start": v(29.32, 26.93) * mm, "end": v(29.34, 25.61) * mm});
            skLineSegment(sketch, "E6.8.0.3", {"start": v(29.34, 25.61) * mm, "end": v(24.37, 22.67) * mm});
            skLineSegment(sketch, "E6.8.0.4", {"start": v(24.37, 22.67) * mm, "end": v(19.34, 25.5) * mm});
            skLineSegment(sketch, "E6.8.0.5", {"start": v(19.34, 25.5) * mm, "end": v(19.27, 31.27) * mm});
            skLineSegment(sketch, "E6.8.0.6", {"start": v(13.28, 20.95) * mm, "end": v(18.28, 23.84) * mm});
            skLineSegment(sketch, "E6.8.0.7", {"start": v(18.28, 23.84) * mm, "end": v(23.28, 20.95) * mm});
            skLineSegment(sketch, "E6.8.0.8", {"start": v(23.28, 20.95) * mm, "end": v(23.28, 15.18) * mm});
            skLineSegment(sketch, "E6.8.0.9", {"start": v(23.28, 15.18) * mm, "end": v(18.28, 12.29) * mm});
            skLineSegment(sketch, "E6.8.0.10", {"start": v(18.28, 12.29) * mm, "end": v(13.28, 15.18) * mm});
            skLineSegment(sketch, "E6.8.0.11", {"start": v(13.28, 15.18) * mm, "end": v(13.28, 20.95) * mm});
            skLineSegment(sketch, "E6.8.1.0", {"start": v(19.27, 10.57) * mm, "end": v(24.24, 13.52) * mm});
            skLineSegment(sketch, "E6.8.1.1", {"start": v(24.24, 13.52) * mm, "end": v(29.27, 10.69) * mm});
            skLineSegment(sketch, "E6.8.1.2", {"start": v(29.27, 10.69) * mm, "end": v(29.34, 4.91) * mm});
            skLineSegment(sketch, "E6.8.1.3", {"start": v(29.34, 4.91) * mm, "end": v(24.37, 1.97) * mm});
            skLineSegment(sketch, "E6.8.1.4", {"start": v(24.37, 1.97) * mm, "end": v(19.34, 4.8) * mm});
            skLineSegment(sketch, "E6.8.1.5", {"start": v(19.34, 4.8) * mm, "end": v(19.27, 10.57) * mm});
            skLineSegment(sketch, "E6.8.1.6", {"start": v(13.28, 0.25) * mm, "end": v(18.28, 3.14) * mm});
            skLineSegment(sketch, "E6.8.1.7", {"start": v(18.28, 3.14) * mm, "end": v(23.28, 0.25) * mm});
            skLineSegment(sketch, "E6.8.1.8", {"start": v(23.28, 0.25) * mm, "end": v(23.28, -5.52) * mm});
            skLineSegment(sketch, "E6.8.1.9", {"start": v(23.28, -5.52) * mm, "end": v(18.28, -8.4) * mm});
            skLineSegment(sketch, "E6.8.1.10", {"start": v(18.28, -8.4) * mm, "end": v(13.28, -5.52) * mm});
            skLineSegment(sketch, "E6.8.1.11", {"start": v(13.28, -5.52) * mm, "end": v(13.28, 0.25) * mm});
            skLineSegment(sketch, "E6.8.2.0", {"start": v(19.27, -10.12) * mm, "end": v(24.24, -7.18) * mm});
            skLineSegment(sketch, "E6.8.2.1", {"start": v(24.24, -7.18) * mm, "end": v(29.27, -10.01) * mm});
            skLineSegment(sketch, "E6.8.2.2", {"start": v(29.27, -10.01) * mm, "end": v(29.34, -15.78) * mm});
            skLineSegment(sketch, "E6.8.2.3", {"start": v(29.34, -15.78) * mm, "end": v(24.37, -18.73) * mm});
            skLineSegment(sketch, "E6.8.2.4", {"start": v(24.37, -18.73) * mm, "end": v(19.34, -15.9) * mm});
            skLineSegment(sketch, "E6.8.2.5", {"start": v(19.34, -15.9) * mm, "end": v(19.27, -10.12) * mm});
            skLineSegment(sketch, "E6.8.2.6", {"start": v(13.28, -20.45) * mm, "end": v(18.28, -17.56) * mm});
            skLineSegment(sketch, "E6.8.2.7", {"start": v(18.28, -17.56) * mm, "end": v(23.28, -20.45) * mm});
            skLineSegment(sketch, "E6.8.2.8", {"start": v(23.28, -20.45) * mm, "end": v(23.28, -26.22) * mm});
            skLineSegment(sketch, "E6.8.2.9", {"start": v(23.28, -26.22) * mm, "end": v(18.28, -29.1) * mm});
            skLineSegment(sketch, "E6.8.2.10", {"start": v(18.28, -29.1) * mm, "end": v(13.28, -26.22) * mm});
            skLineSegment(sketch, "E6.8.2.11", {"start": v(13.28, -26.22) * mm, "end": v(13.28, -20.45) * mm});
            skLineSegment(sketch, "E6.8.3.0", {"start": v(19.27, -30.82) * mm, "end": v(24.24, -27.88) * mm});
            skLineSegment(sketch, "E6.8.3.1", {"start": v(24.24, -27.88) * mm, "end": v(25.85, -28.79) * mm});
            skLineSegment(sketch, "E6.8.3.6", {"start": v(13.28, -41.14) * mm, "end": v(18.28, -38.26) * mm});
            skLineSegment(sketch, "E6.8.3.7", {"start": v(18.28, -38.26) * mm, "end": v(23.28, -41.14) * mm});
            skLineSegment(sketch, "E6.8.3.8", {"start": v(23.28, -41.14) * mm, "end": v(23.28, -46.92) * mm});
            skLineSegment(sketch, "E6.8.3.9", {"start": v(23.28, -46.92) * mm, "end": v(18.28, -49.8) * mm});
            skLineSegment(sketch, "E6.8.3.10", {"start": v(18.28, -49.8) * mm, "end": v(13.28, -46.92) * mm});
            skLineSegment(sketch, "E6.8.3.11", {"start": v(13.28, -46.92) * mm, "end": v(13.28, -41.14) * mm});
            skLineSegment(sketch, "E6.9.0.6", {"start": v(25.28, 20.95) * mm, "end": v(30.28, 23.84) * mm});
            skLineSegment(sketch, "E6.9.0.7", {"start": v(30.28, 23.84) * mm, "end": v(35.28, 20.95) * mm});
            skLineSegment(sketch, "E6.9.0.8", {"start": v(35.28, 20.95) * mm, "end": v(35.28, 15.18) * mm});
            skLineSegment(sketch, "E6.9.0.9", {"start": v(35.28, 15.18) * mm, "end": v(30.28, 12.29) * mm});
            skLineSegment(sketch, "E6.9.0.10", {"start": v(30.28, 12.29) * mm, "end": v(25.28, 15.18) * mm});
            skLineSegment(sketch, "E6.9.0.11", {"start": v(25.28, 15.18) * mm, "end": v(25.28, 20.95) * mm});
            skLineSegment(sketch, "E6.9.1.0", {"start": v(31.27, 10.57) * mm, "end": v(36.24, 13.52) * mm});
            skLineSegment(sketch, "E6.9.1.1", {"start": v(36.24, 13.52) * mm, "end": v(41.27, 10.69) * mm});
            skLineSegment(sketch, "E6.9.1.2", {"start": v(41.27, 10.69) * mm, "end": v(41.34, 4.91) * mm});
            skLineSegment(sketch, "E6.9.1.3", {"start": v(41.34, 4.91) * mm, "end": v(36.37, 1.97) * mm});
            skLineSegment(sketch, "E6.9.1.4", {"start": v(36.37, 1.97) * mm, "end": v(31.34, 4.8) * mm});
            skLineSegment(sketch, "E6.9.1.5", {"start": v(31.34, 4.8) * mm, "end": v(31.27, 10.57) * mm});
            skLineSegment(sketch, "E6.9.1.6", {"start": v(25.28, 0.25) * mm, "end": v(30.28, 3.14) * mm});
            skLineSegment(sketch, "E6.9.1.7", {"start": v(30.28, 3.14) * mm, "end": v(35.28, 0.25) * mm});
            skLineSegment(sketch, "E6.9.1.8", {"start": v(35.28, 0.25) * mm, "end": v(35.28, -5.52) * mm});
            skLineSegment(sketch, "E6.9.1.9", {"start": v(35.28, -5.52) * mm, "end": v(30.28, -8.4) * mm});
            skLineSegment(sketch, "E6.9.1.10", {"start": v(30.28, -8.4) * mm, "end": v(25.28, -5.52) * mm});
            skLineSegment(sketch, "E6.9.1.11", {"start": v(25.28, -5.52) * mm, "end": v(25.28, 0.25) * mm});
            skLineSegment(sketch, "E6.9.2.0", {"start": v(31.27, -10.12) * mm, "end": v(36.24, -7.18) * mm});
            skLineSegment(sketch, "E6.9.2.1", {"start": v(36.24, -7.18) * mm, "end": v(41.27, -10.01) * mm});
            skLineSegment(sketch, "E6.9.2.2", {"start": v(41.27, -10.01) * mm, "end": v(41.34, -15.78) * mm});
            skLineSegment(sketch, "E6.9.2.3", {"start": v(41.34, -15.78) * mm, "end": v(36.37, -18.73) * mm});
            skLineSegment(sketch, "E6.9.2.4", {"start": v(36.37, -18.73) * mm, "end": v(31.34, -15.9) * mm});
            skLineSegment(sketch, "E6.9.2.5", {"start": v(31.34, -15.9) * mm, "end": v(31.27, -10.12) * mm});
            skLineSegment(sketch, "E6.9.2.6", {"start": v(25.28, -20.45) * mm, "end": v(30.28, -17.56) * mm});
            skLineSegment(sketch, "E6.9.2.7", {"start": v(30.28, -17.56) * mm, "end": v(35.28, -20.45) * mm});
            skLineSegment(sketch, "E6.9.2.8", {"start": v(35.28, -20.45) * mm, "end": v(35.28, -22.75) * mm});
            skLineSegment(sketch, "E6.9.2.10", {"start": v(27.9, -27.73) * mm, "end": v(25.28, -26.22) * mm});
            skLineSegment(sketch, "E6.9.2.11", {"start": v(25.28, -26.22) * mm, "end": v(25.28, -20.45) * mm});
            skLineSegment(sketch, "E6.9.3.0", {"start": v(31.27, -30.82) * mm, "end": v(36.24, -27.88) * mm});
            skLineSegment(sketch, "E6.9.3.1", {"start": v(36.24, -27.88) * mm, "end": v(41.27, -30.7) * mm});
            skLineSegment(sketch, "E6.9.3.2", {"start": v(41.27, -30.7) * mm, "end": v(41.34, -36.48) * mm});
            skLineSegment(sketch, "E6.9.3.3", {"start": v(41.34, -36.48) * mm, "end": v(36.37, -39.42) * mm});
            skLineSegment(sketch, "E6.9.3.4", {"start": v(36.37, -39.42) * mm, "end": v(31.34, -36.6) * mm});
            skLineSegment(sketch, "E6.9.3.5", {"start": v(31.34, -36.6) * mm, "end": v(31.27, -30.82) * mm});
            skLineSegment(sketch, "E6.9.3.6", {"start": v(25.28, -41.14) * mm, "end": v(30.28, -38.26) * mm});
            skLineSegment(sketch, "E6.9.3.7", {"start": v(30.28, -38.26) * mm, "end": v(35.28, -41.14) * mm});
            skLineSegment(sketch, "E6.9.3.8", {"start": v(35.28, -41.14) * mm, "end": v(35.28, -46.92) * mm});
            skLineSegment(sketch, "E6.9.3.9", {"start": v(35.28, -46.92) * mm, "end": v(30.28, -49.8) * mm});
            skLineSegment(sketch, "E6.9.3.10", {"start": v(30.28, -49.8) * mm, "end": v(25.28, -46.92) * mm});
            skLineSegment(sketch, "E6.9.3.11", {"start": v(25.28, -46.92) * mm, "end": v(25.28, -41.14) * mm});
            skLineSegment(sketch, "E6.10.0.0", {"start": v(43.27, 31.27) * mm, "end": v(48.24, 34.22) * mm});
            skLineSegment(sketch, "E6.10.0.1", {"start": v(48.24, 34.22) * mm, "end": v(53.27, 31.39) * mm});
            skLineSegment(sketch, "E6.10.0.2", {"start": v(53.27, 31.39) * mm, "end": v(53.34, 25.61) * mm});
            skLineSegment(sketch, "E6.10.0.3", {"start": v(53.34, 25.61) * mm, "end": v(48.37, 22.67) * mm});
            skLineSegment(sketch, "E6.10.0.4", {"start": v(48.37, 22.67) * mm, "end": v(43.34, 25.5) * mm});
            skLineSegment(sketch, "E6.10.0.5", {"start": v(43.34, 25.5) * mm, "end": v(43.27, 31.27) * mm});
            skLineSegment(sketch, "E6.10.0.6", {"start": v(37.28, 20.95) * mm, "end": v(37.3, 20.95) * mm});
            skLineSegment(sketch, "E6.10.0.10", {"start": v(42.28, 12.29) * mm, "end": v(37.28, 15.18) * mm});
            skLineSegment(sketch, "E6.10.0.11", {"start": v(37.28, 15.18) * mm, "end": v(37.28, 20.95) * mm});
            skLineSegment(sketch, "E6.10.1.0", {"start": v(43.27, 10.57) * mm, "end": v(44.41, 11.25) * mm});
            skLineSegment(sketch, "E6.10.1.1", {"start": v(48.24, 13.52) * mm, "end": v(53.27, 10.69) * mm});
            skLineSegment(sketch, "E6.10.1.2", {"start": v(53.27, 10.69) * mm, "end": v(53.34, 4.91) * mm});
            skLineSegment(sketch, "E6.10.1.4", {"start": v(46.84, 2.83) * mm, "end": v(43.34, 4.8) * mm});
            skLineSegment(sketch, "E6.10.1.5", {"start": v(43.34, 4.8) * mm, "end": v(43.27, 10.57) * mm});
            skLineSegment(sketch, "E6.10.1.6", {"start": v(37.28, 0.25) * mm, "end": v(42.28, 3.14) * mm});
            skLineSegment(sketch, "E6.10.1.7", {"start": v(42.28, 3.14) * mm, "end": v(47, 0.42) * mm});
            skLineSegment(sketch, "E6.10.1.9", {"start": v(46.25, -6.12) * mm, "end": v(42.28, -8.4) * mm});
            skLineSegment(sketch, "E6.10.1.10", {"start": v(42.28, -8.4) * mm, "end": v(37.28, -5.52) * mm});
            skLineSegment(sketch, "E6.10.1.11", {"start": v(37.28, -5.52) * mm, "end": v(37.28, 0.25) * mm});
            skLineSegment(sketch, "E6.10.2.0", {"start": v(43.27, -10.12) * mm, "end": v(45.41, -8.86) * mm});
            skLineSegment(sketch, "E6.10.2.5", {"start": v(43.3, -13.36) * mm, "end": v(43.27, -10.12) * mm});
            skLineSegment(sketch, "E6.10.3.0", {"start": v(43.27, -30.82) * mm, "end": v(48.24, -27.88) * mm});
            skLineSegment(sketch, "E6.10.3.1", {"start": v(48.24, -27.88) * mm, "end": v(53.27, -30.7) * mm});
            skLineSegment(sketch, "E6.10.3.2", {"start": v(53.27, -30.7) * mm, "end": v(53.34, -36.48) * mm});
            skLineSegment(sketch, "E6.10.3.3", {"start": v(53.34, -36.48) * mm, "end": v(48.37, -39.42) * mm});
            skLineSegment(sketch, "E6.10.3.4", {"start": v(48.37, -39.42) * mm, "end": v(43.34, -36.6) * mm});
            skLineSegment(sketch, "E6.10.3.5", {"start": v(43.34, -36.6) * mm, "end": v(43.27, -30.82) * mm});
            skLineSegment(sketch, "E6.10.3.6", {"start": v(37.28, -41.14) * mm, "end": v(42.28, -38.26) * mm});
            skLineSegment(sketch, "E6.10.3.7", {"start": v(42.28, -38.26) * mm, "end": v(47.28, -41.14) * mm});
            skLineSegment(sketch, "E6.10.3.8", {"start": v(47.28, -41.14) * mm, "end": v(47.28, -46.92) * mm});
            skLineSegment(sketch, "E6.10.3.9", {"start": v(47.28, -46.92) * mm, "end": v(42.28, -49.8) * mm});
            skLineSegment(sketch, "E6.10.3.10", {"start": v(42.28, -49.8) * mm, "end": v(37.28, -46.92) * mm});
            skLineSegment(sketch, "E6.10.3.11", {"start": v(37.28, -46.92) * mm, "end": v(37.28, -41.14) * mm});
            skLineSegment(sketch, "E6.11.0.0", {"start": v(55.27, 31.27) * mm, "end": v(60.24, 34.22) * mm});
            skLineSegment(sketch, "E6.11.0.1", {"start": v(60.24, 34.22) * mm, "end": v(65.27, 31.39) * mm});
            skLineSegment(sketch, "E6.11.0.2", {"start": v(65.27, 31.39) * mm, "end": v(65.34, 25.61) * mm});
            skLineSegment(sketch, "E6.11.0.3", {"start": v(65.34, 25.61) * mm, "end": v(60.37, 22.67) * mm});
            skLineSegment(sketch, "E6.11.0.4", {"start": v(60.37, 22.67) * mm, "end": v(55.34, 25.5) * mm});
            skLineSegment(sketch, "E6.11.0.5", {"start": v(55.34, 25.5) * mm, "end": v(55.27, 31.27) * mm});
            skLineSegment(sketch, "E6.11.0.6", {"start": v(49.28, 20.95) * mm, "end": v(54.28, 23.84) * mm});
            skLineSegment(sketch, "E6.11.0.7", {"start": v(54.28, 23.84) * mm, "end": v(59.28, 20.95) * mm});
            skLineSegment(sketch, "E6.11.0.8", {"start": v(59.28, 20.95) * mm, "end": v(59.28, 15.18) * mm});
            skLineSegment(sketch, "E6.11.0.9", {"start": v(59.28, 15.18) * mm, "end": v(54.28, 12.29) * mm});
            skLineSegment(sketch, "E6.11.0.10", {"start": v(54.28, 12.29) * mm, "end": v(49.28, 15.18) * mm});
            skLineSegment(sketch, "E6.11.0.11", {"start": v(49.28, 15.18) * mm, "end": v(49.28, 20.95) * mm});
            skLineSegment(sketch, "E6.11.1.0", {"start": v(55.27, 10.57) * mm, "end": v(60.24, 13.52) * mm});
            skLineSegment(sketch, "E6.11.1.1", {"start": v(60.24, 13.52) * mm, "end": v(65.27, 10.69) * mm});
            skLineSegment(sketch, "E6.11.1.2", {"start": v(65.27, 10.69) * mm, "end": v(65.34, 4.91) * mm});
            skLineSegment(sketch, "E6.11.1.3", {"start": v(65.34, 4.91) * mm, "end": v(60.37, 1.97) * mm});
            skLineSegment(sketch, "E6.11.1.4", {"start": v(60.37, 1.97) * mm, "end": v(55.34, 4.8) * mm});
            skLineSegment(sketch, "E6.11.1.5", {"start": v(55.34, 4.8) * mm, "end": v(55.27, 10.57) * mm});
            skLineSegment(sketch, "E6.11.1.7", {"start": v(54.28, 3.14) * mm, "end": v(59.28, 0.25) * mm});
            skLineSegment(sketch, "E6.11.1.8", {"start": v(59.28, 0.25) * mm, "end": v(59.28, -5.52) * mm});
            skLineSegment(sketch, "E6.11.1.9", {"start": v(59.28, -5.52) * mm, "end": v(54.28, -8.4) * mm});
            skLineSegment(sketch, "E6.11.2.0", {"start": v(55.27, -10.12) * mm, "end": v(60.24, -7.18) * mm});
            skLineSegment(sketch, "E6.11.2.1", {"start": v(60.24, -7.18) * mm, "end": v(65.27, -10.01) * mm});
            skLineSegment(sketch, "E6.11.2.2", {"start": v(65.27, -10.01) * mm, "end": v(65.34, -15.78) * mm});
            skLineSegment(sketch, "E6.11.2.3", {"start": v(65.34, -15.78) * mm, "end": v(60.37, -18.73) * mm});
            skLineSegment(sketch, "E6.11.2.4", {"start": v(60.37, -18.73) * mm, "end": v(55.34, -15.9) * mm});
            skLineSegment(sketch, "E6.11.2.5", {"start": v(55.34, -15.9) * mm, "end": v(55.27, -10.12) * mm});
            skLineSegment(sketch, "E6.11.2.6", {"start": v(49.28, -20.45) * mm, "end": v(54.28, -17.56) * mm});
            skLineSegment(sketch, "E6.11.2.7", {"start": v(54.28, -17.56) * mm, "end": v(59.28, -20.45) * mm});
            skLineSegment(sketch, "E6.11.2.8", {"start": v(59.28, -20.45) * mm, "end": v(59.28, -26.22) * mm});
            skLineSegment(sketch, "E6.11.2.9", {"start": v(59.28, -26.22) * mm, "end": v(54.28, -29.1) * mm});
            skLineSegment(sketch, "E6.11.2.10", {"start": v(54.28, -29.1) * mm, "end": v(49.28, -26.22) * mm});
            skLineSegment(sketch, "E6.11.2.11", {"start": v(49.28, -26.22) * mm, "end": v(49.28, -20.45) * mm});
            skLineSegment(sketch, "E6.11.3.0", {"start": v(55.27, -30.82) * mm, "end": v(60.24, -27.88) * mm});
            skLineSegment(sketch, "E6.11.3.1", {"start": v(60.24, -27.88) * mm, "end": v(65.27, -30.7) * mm});
            skLineSegment(sketch, "E6.11.3.2", {"start": v(65.27, -30.7) * mm, "end": v(65.34, -36.48) * mm});
            skLineSegment(sketch, "E6.11.3.3", {"start": v(65.34, -36.48) * mm, "end": v(60.37, -39.42) * mm});
            skLineSegment(sketch, "E6.11.3.4", {"start": v(60.37, -39.42) * mm, "end": v(55.34, -36.6) * mm});
            skLineSegment(sketch, "E6.11.3.5", {"start": v(55.34, -36.6) * mm, "end": v(55.27, -30.82) * mm});
            skLineSegment(sketch, "E6.11.3.6", {"start": v(49.28, -41.14) * mm, "end": v(54.28, -38.26) * mm});
            skLineSegment(sketch, "E6.11.3.7", {"start": v(54.28, -38.26) * mm, "end": v(59.28, -41.14) * mm});
            skLineSegment(sketch, "E6.11.3.8", {"start": v(59.28, -41.14) * mm, "end": v(59.28, -46.92) * mm});
            skLineSegment(sketch, "E6.11.3.9", {"start": v(59.28, -46.92) * mm, "end": v(54.28, -49.8) * mm});
            skLineSegment(sketch, "E6.11.3.10", {"start": v(54.28, -49.8) * mm, "end": v(49.28, -46.92) * mm});
            skLineSegment(sketch, "E6.11.3.11", {"start": v(49.28, -46.92) * mm, "end": v(49.28, -41.14) * mm});
            skLineSegment(sketch, "E6.direction1", {"start": v(-76.73, 31.27) * mm, "end": v(-64.73, 31.27) * mm, "construction": true});
            skLineSegment(sketch, "E6.direction2", {"start": v(-76.73, 31.27) * mm, "end": v(-76.73, 10.57) * mm, "construction": true});
            skLineSegment(sketch, "E7.trimOffspring", {"start": v(-19, 31.54) * mm, "end": v(-18.73, 31.39) * mm});
            skPoint(sketch, "E8.orphan", {"position": v(-11.76, 34.22) * mm});
            skLineSegment(sketch, "E9", {"start": v(-10.66, 33.6) * mm, "end": v(-13.9, 32.95) * mm});
            skPoint(sketch, "E10.orphan", {"position": v(12.24, 34.22) * mm});
            skPoint(sketch, "E11.orphan", {"position": v(29.27, 31.39) * mm});
            skLineSegment(sketch, "E12.trimOffspring", {"start": v(43.51, 13) * mm, "end": v(42.28, 12.29) * mm});
            skLineSegment(sketch, "E13", {"start": v(37.3, 20.95) * mm, "end": v(37.85, 20.42) * mm});
            skFitSpline(sketch, "E14.trimOffspring", {"points": [v(-46.96, 1.66) * mm, v(-47.02, 0) * mm, v(-46.96, -1.66) * mm, v(-46.74, -3.86) * mm, v(-46.2, -6.59) * mm, v(-45.13, -9.8) * mm, v(-43.64, -12.92) * mm, v(-41.73, -15.94) * mm, v(-39.42, -18.84) * mm, v(-37.17, -21.13) * mm, v(-35.17, -22.87) * mm, v(-33.57, -24.13) * mm, v(-31.89, -25.33) * mm, v(-29.54, -26.84) * mm, v(-26.44, -28.56) * mm, v(-22.47, -30.35) * mm, v(-18.27, -31.83) * mm, v(-13.9, -33) * mm, v(-9.37, -33.86) * mm, v(-5.5, -34.3) * mm, v(-2.37, -34.47) * mm, v(0, -34.51) * mm, v(2.37, -34.47) * mm, v(5.5, -34.3) * mm, v(9.37, -33.86) * mm, v(13.9, -33) * mm, v(18.27, -31.83) * mm, v(22.47, -30.35) * mm, v(26.44, -28.56) * mm, v(29.54, -26.84) * mm, v(31.89, -25.33) * mm, v(33.57, -24.13) * mm, v(35.17, -22.87) * mm, v(37.17, -21.13) * mm, v(39.42, -18.84) * mm, v(41.73, -15.94) * mm, v(43.64, -12.92) * mm, v(45.13, -9.8) * mm, v(46.2, -6.59) * mm, v(46.74, -3.86) * mm, v(46.96, -1.66) * mm, v(47.02, 0) * mm, v(46.96, 1.66) * mm, v(46.74, 3.86) * mm, v(46.2, 6.59) * mm, v(45.13, 9.8) * mm, v(43.64, 12.92) * mm, v(41.73, 15.94) * mm, v(39.42, 18.84) * mm, v(37.17, 21.13) * mm, v(35.17, 22.87) * mm, v(33.57, 24.13) * mm, v(31.89, 25.33) * mm, v(29.54, 26.84) * mm, v(26.44, 28.56) * mm, v(22.47, 30.35) * mm, v(18.27, 31.83) * mm, v(13.9, 33) * mm, v(9.37, 33.86) * mm, v(5.5, 34.3) * mm, v(2.37, 34.47) * mm, v(0, 34.51) * mm, v(-2.37, 34.47) * mm, v(-5.5, 34.3) * mm, v(-9.37, 33.86) * mm, v(-13.9, 33) * mm, v(-18.27, 31.83) * mm, v(-22.47, 30.35) * mm, v(-26.44, 28.56) * mm, v(-29.54, 26.84) * mm, v(-31.89, 25.33) * mm, v(-33.57, 24.13) * mm, v(-35.17, 22.87) * mm, v(-37.17, 21.13) * mm, v(-39.42, 18.84) * mm, v(-41.73, 15.94) * mm, v(-43.64, 12.92) * mm, v(-45.13, 9.8) * mm, v(-46.2, 6.59) * mm, v(-46.74, 3.86) * mm, v(-46.96, 1.66) * mm, v(-47.02, 0) * mm, v(-46.96, -1.66) * mm]});
            skLineSegment(sketch, "E15", {"start": v(-30.67, 26.1) * mm, "end": v(-30.67, 26.1) * mm});
            skLineSegment(sketch, "E16", {"start": v(-31.47, 25.6) * mm, "end": v(-31.45, 25.6) * mm});
            skLineSegment(sketch, "E17", {"start": v(-28.68, 27.3) * mm, "end": v(-19, 31.54) * mm});
            skLineSegment(sketch, "E18.trimOffspring", {"start": v(-44.27, 11.55) * mm, "end": v(-42.73, 10.69) * mm});
            skPoint(sketch, "E19.orphan", {"position": v(-47.63, 1.97) * mm});
            skPoint(sketch, "E20.orphan", {"position": v(-48.72, -5.52) * mm});
            skPoint(sketch, "E21.orphan", {"position": v(-46.72, -5.52) * mm});
            skPoint(sketch, "E22.orphan", {"position": v(-47.76, -7.18) * mm});
            skPoint(sketch, "E23.orphan", {"position": v(-42.66, -15.78) * mm});
            skPoint(sketch, "E24.orphan", {"position": v(-41.72, -17.56) * mm});
            skPoint(sketch, "E25.orphan", {"position": v(-29.72, -29.1) * mm});
            skLineSegment(sketch, "E26.trimOffspring", {"start": v(-25.54, -28.93) * mm, "end": v(-23.76, -27.88) * mm});
            skLineSegment(sketch, "E27.trimOffspring", {"start": v(-16.71, -32.23) * mm, "end": v(-16.73, -30.82) * mm});
            skLineSegment(sketch, "E28.trimOffspring", {"start": v(19.28, -31.45) * mm, "end": v(19.27, -30.82) * mm});
            skPoint(sketch, "E29.orphan", {"position": v(43.34, -15.9) * mm});
            skPoint(sketch, "E30.orphan", {"position": v(48.24, -7.18) * mm});
            skPoint(sketch, "E31.orphan", {"position": v(49.28, 0.25) * mm});
            skPoint(sketch, "E32.orphan", {"position": v(47.28, 0.25) * mm});
            skPoint(sketch, "E33.orphan", {"position": v(48.37, 1.97) * mm});
            skLineSegment(sketch, "E34", {"start": v(-44.27, 11.55) * mm, "end": v(-46.88, 2.41) * mm});
            skLineSegment(sketch, "E35", {"start": v(-36.72, 20.95) * mm, "end": v(-37.01, 21.2) * mm});
            skLineSegment(sketch, "E36", {"start": v(-43.37, 13.25) * mm, "end": v(-37.01, 21.2) * mm});
            skLineSegment(sketch, "E37", {"start": v(11.07, 33.52) * mm, "end": v(14.93, 32.7) * mm});
            skLineSegment(sketch, "E38", {"start": v(29.32, 26.93) * mm, "end": v(19.47, 31.39) * mm});
            skLineSegment(sketch, "E39", {"start": v(-46.72, -3.77) * mm, "end": v(-46.34, -5.74) * mm});
            skLineSegment(sketch, "E40", {"start": v(-34.72, -23.21) * mm, "end": v(-27.6, -27.89) * mm});
            skLineSegment(sketch, "E41", {"start": v(-25.54, -28.93) * mm, "end": v(-18.72, -31.63) * mm});
            skLineSegment(sketch, "E42", {"start": v(-16.71, -32.23) * mm, "end": v(-6.69, -34.15) * mm});
            skLineSegment(sketch, "E43", {"start": v(-4.69, -34.33) * mm, "end": v(5.31, -34.28) * mm});
            skLineSegment(sketch, "E44", {"start": v(7.3, -34.08) * mm, "end": v(17.29, -32.07) * mm});
            skLineSegment(sketch, "E45", {"start": v(19.28, -31.45) * mm, "end": v(25.85, -28.79) * mm});
            skLineSegment(sketch, "E46", {"start": v(27.9, -27.73) * mm, "end": v(35.28, -22.75) * mm});
            skLineSegment(sketch, "E47", {"start": v(43.3, -13.36) * mm, "end": v(45.41, -8.86) * mm});
            skLineSegment(sketch, "E48", {"start": v(46.25, -6.12) * mm, "end": v(47, 0.42) * mm});
            skLineSegment(sketch, "E49", {"start": v(46.84, 2.83) * mm, "end": v(44.41, 11.25) * mm});
            skSolve(sketch);
        }
        {
            var Q0;
            Q0=makeQuery(id+"F0.imprint","IMPRINT",FACE,{"disambiguationData":[TD([[makeQuery(id+"F0.imprint","IMPRINT",EDGE,{"derivedFrom":sQuery(id+"F0.wireOp",EDGE,"E0")}),1.0]])]});
            extrude(context, id + "F1", {"entities" : qUnion([Q0]), "depth" : 1.5 * mm});
        }
        {
            var Q0;
            Q0=makeQuery(id+"F1.opExtrude","CAP_FACE",FACE,{"disambiguationData":[OSD([sQuery(id+"F0.wireOp",EDGE,"E0"),sQuery(id+"F0.wireOp",EDGE,"E6.2.1.2"),sQuery(id+"F0.wireOp",EDGE,"E6.2.1.3"),sQuery(id+"F0.wireOp",EDGE,"E6.3.0.8"),sQuery(id+"F0.wireOp",EDGE,"E6.3.0.9"),sQuery(id+"F0.wireOp",EDGE,"E6.3.0.10"),sQuery(id+"F0.wireOp",EDGE,"E6.3.1.0"),sQuery(id+"F0.wireOp",EDGE,"E6.3.1.1"),sQuery(id+"F0.wireOp",EDGE,"E6.3.1.2"),sQuery(id+"F0.wireOp",EDGE,"E6.3.1.3"),sQuery(id+"F0.wireOp",EDGE,"E6.3.1.4"),sQuery(id+"F0.wireOp",EDGE,"E6.3.1.5"),sQuery(id+"F0.wireOp",EDGE,"E6.3.1.6"),sQuery(id+"F0.wireOp",EDGE,"E6.3.1.7"),sQuery(id+"F0.wireOp",EDGE,"E6.3.1.8"),sQuery(id+"F0.wireOp",EDGE,"E6.3.1.9"),sQuery(id+"F0.wireOp",EDGE,"E6.3.1.10"),sQuery(id+"F0.wireOp",EDGE,"E6.3.1.11"),sQuery(id+"F0.wireOp",EDGE,"E6.3.2.0"),sQuery(id+"F0.wireOp",EDGE,"E6.3.2.1"),sQuery(id+"F0.wireOp",EDGE,"E6.3.2.2"),sQuery(id+"F0.wireOp",EDGE,"E6.3.2.3"),sQuery(id+"F0.wireOp",EDGE,"E6.3.2.4"),sQuery(id+"F0.wireOp",EDGE,"E6.3.2.5"),sQuery(id+"F0.wireOp",EDGE,"E6.4.0.2"),sQuery(id+"F0.wireOp",EDGE,"E6.4.0.3"),sQuery(id+"F0.wireOp",EDGE,"E6.4.0.4"),sQuery(id+"F0.wireOp",EDGE,"E6.4.0.5"),sQuery(id+"F0.wireOp",EDGE,"E6.4.0.6"),sQuery(id+"F0.wireOp",EDGE,"E6.4.0.7"),sQuery(id+"F0.wireOp",EDGE,"E6.4.0.8"),sQuery(id+"F0.wireOp",EDGE,"E6.4.0.9"),sQuery(id+"F0.wireOp",EDGE,"E6.4.0.10"),sQuery(id+"F0.wireOp",EDGE,"E6.4.0.11"),sQuery(id+"F0.wireOp",EDGE,"E6.4.1.0"),sQuery(id+"F0.wireOp",EDGE,"E6.4.1.1"),sQuery(id+"F0.wireOp",EDGE,"E6.4.1.2"),sQuery(id+"F0.wireOp",EDGE,"E6.4.1.3"),sQuery(id+"F0.wireOp",EDGE,"E6.4.1.4"),sQuery(id+"F0.wireOp",EDGE,"E6.4.1.5"),sQuery(id+"F0.wireOp",EDGE,"E6.4.1.6"),sQuery(id+"F0.wireOp",EDGE,"E6.4.1.7"),sQuery(id+"F0.wireOp",EDGE,"E6.4.1.8"),sQuery(id+"F0.wireOp",EDGE,"E6.4.1.9"),sQuery(id+"F0.wireOp",EDGE,"E6.4.1.10"),sQuery(id+"F0.wireOp",EDGE,"E6.4.1.11"),sQuery(id+"F0.wireOp",EDGE,"E6.4.2.0"),sQuery(id+"F0.wireOp",EDGE,"E6.4.2.1"),sQuery(id+"F0.wireOp",EDGE,"E6.4.2.2"),sQuery(id+"F0.wireOp",EDGE,"E6.4.2.3"),sQuery(id+"F0.wireOp",EDGE,"E6.4.2.4"),sQuery(id+"F0.wireOp",EDGE,"E6.4.2.5"),sQuery(id+"F0.wireOp",EDGE,"E6.4.2.6"),sQuery(id+"F0.wireOp",EDGE,"E6.4.2.7"),sQuery(id+"F0.wireOp",EDGE,"E6.4.2.8"),sQuery(id+"F0.wireOp",EDGE,"E6.4.2.9"),sQuery(id+"F0.wireOp",EDGE,"E6.4.2.11"),sQuery(id+"F0.wireOp",EDGE,"E6.4.3.1"),sQuery(id+"F0.wireOp",EDGE,"E6.4.3.2"),sQuery(id+"F0.wireOp",EDGE,"E6.5.0.0"),sQuery(id+"F0.wireOp",EDGE,"E6.5.0.1"),sQuery(id+"F0.wireOp",EDGE,"E6.5.0.2"),sQuery(id+"F0.wireOp",EDGE,"E6.5.0.3"),sQuery(id+"F0.wireOp",EDGE,"E6.5.0.4"),sQuery(id+"F0.wireOp",EDGE,"E6.5.0.5"),sQuery(id+"F0.wireOp",EDGE,"E6.5.0.6"),sQuery(id+"F0.wireOp",EDGE,"E6.5.0.7"),sQuery(id+"F0.wireOp",EDGE,"E6.5.0.8"),sQuery(id+"F0.wireOp",EDGE,"E6.5.0.9"),sQuery(id+"F0.wireOp",EDGE,"E6.5.0.10"),sQuery(id+"F0.wireOp",EDGE,"E6.5.0.11"),sQuery(id+"F0.wireOp",EDGE,"E6.5.1.0"),sQuery(id+"F0.wireOp",EDGE,"E6.5.1.1"),sQuery(id+"F0.wireOp",EDGE,"E6.5.1.2"),sQuery(id+"F0.wireOp",EDGE,"E6.5.1.3"),sQuery(id+"F0.wireOp",EDGE,"E6.5.1.4"),sQuery(id+"F0.wireOp",EDGE,"E6.5.1.5"),sQuery(id+"F0.wireOp",EDGE,"E6.5.1.6"),sQuery(id+"F0.wireOp",EDGE,"E6.5.1.7"),sQuery(id+"F0.wireOp",EDGE,"E6.5.1.8"),sQuery(id+"F0.wireOp",EDGE,"E6.5.1.9"),sQuery(id+"F0.wireOp",EDGE,"E6.5.1.10"),sQuery(id+"F0.wireOp",EDGE,"E6.5.1.11"),sQuery(id+"F0.wireOp",EDGE,"E6.5.2.0"),sQuery(id+"F0.wireOp",EDGE,"E6.5.2.1"),sQuery(id+"F0.wireOp",EDGE,"E6.5.2.2"),sQuery(id+"F0.wireOp",EDGE,"E6.5.2.3"),sQuery(id+"F0.wireOp",EDGE,"E6.5.2.4"),sQuery(id+"F0.wireOp",EDGE,"E6.5.2.5"),sQuery(id+"F0.wireOp",EDGE,"E6.5.2.6"),sQuery(id+"F0.wireOp",EDGE,"E6.5.2.7"),sQuery(id+"F0.wireOp",EDGE,"E6.5.2.8"),sQuery(id+"F0.wireOp",EDGE,"E6.5.2.9"),sQuery(id+"F0.wireOp",EDGE,"E6.5.2.10"),sQuery(id+"F0.wireOp",EDGE,"E6.5.2.11"),sQuery(id+"F0.wireOp",EDGE,"E6.5.3.0"),sQuery(id+"F0.wireOp",EDGE,"E6.5.3.1"),sQuery(id+"F0.wireOp",EDGE,"E6.5.3.2"),sQuery(id+"F0.wireOp",EDGE,"E6.6.0.0"),sQuery(id+"F0.wireOp",EDGE,"E6.6.0.1"),sQuery(id+"F0.wireOp",EDGE,"E6.6.0.2"),sQuery(id+"F0.wireOp",EDGE,"E6.6.0.3"),sQuery(id+"F0.wireOp",EDGE,"E6.6.0.4"),sQuery(id+"F0.wireOp",EDGE,"E6.6.0.5"),sQuery(id+"F0.wireOp",EDGE,"E6.6.0.6"),sQuery(id+"F0.wireOp",EDGE,"E6.6.0.7"),sQuery(id+"F0.wireOp",EDGE,"E6.6.0.8"),sQuery(id+"F0.wireOp",EDGE,"E6.6.0.9"),sQuery(id+"F0.wireOp",EDGE,"E6.6.0.10"),sQuery(id+"F0.wireOp",EDGE,"E6.6.0.11"),sQuery(id+"F0.wireOp",EDGE,"E6.6.1.0"),sQuery(id+"F0.wireOp",EDGE,"E6.6.1.1"),sQuery(id+"F0.wireOp",EDGE,"E6.6.1.2"),sQuery(id+"F0.wireOp",EDGE,"E6.6.1.3"),sQuery(id+"F0.wireOp",EDGE,"E6.6.1.4"),sQuery(id+"F0.wireOp",EDGE,"E6.6.1.5"),sQuery(id+"F0.wireOp",EDGE,"E6.6.1.6"),sQuery(id+"F0.wireOp",EDGE,"E6.6.1.7"),sQuery(id+"F0.wireOp",EDGE,"E6.6.1.8"),sQuery(id+"F0.wireOp",EDGE,"E6.6.1.9"),sQuery(id+"F0.wireOp",EDGE,"E6.6.1.10"),sQuery(id+"F0.wireOp",EDGE,"E6.6.1.11"),sQuery(id+"F0.wireOp",EDGE,"E6.6.2.0"),sQuery(id+"F0.wireOp",EDGE,"E6.6.2.1"),sQuery(id+"F0.wireOp",EDGE,"E6.6.2.2"),sQuery(id+"F0.wireOp",EDGE,"E6.6.2.3"),sQuery(id+"F0.wireOp",EDGE,"E6.6.2.4"),sQuery(id+"F0.wireOp",EDGE,"E6.6.2.5"),sQuery(id+"F0.wireOp",EDGE,"E6.6.2.6"),sQuery(id+"F0.wireOp",EDGE,"E6.6.2.7"),sQuery(id+"F0.wireOp",EDGE,"E6.6.2.8"),sQuery(id+"F0.wireOp",EDGE,"E6.6.2.9"),sQuery(id+"F0.wireOp",EDGE,"E6.6.2.10"),sQuery(id+"F0.wireOp",EDGE,"E6.6.2.11"),sQuery(id+"F0.wireOp",EDGE,"E6.6.3.0"),sQuery(id+"F0.wireOp",EDGE,"E6.6.3.1"),sQuery(id+"F0.wireOp",EDGE,"E6.6.3.2"),sQuery(id+"F0.wireOp",EDGE,"E6.6.3.5"),sQuery(id+"F0.wireOp",EDGE,"E6.7.0.0"),sQuery(id+"F0.wireOp",EDGE,"E6.7.0.1"),sQuery(id+"F0.wireOp",EDGE,"E6.7.0.2"),sQuery(id+"F0.wireOp",EDGE,"E6.7.0.3"),sQuery(id+"F0.wireOp",EDGE,"E6.7.0.4"),sQuery(id+"F0.wireOp",EDGE,"E6.7.0.5"),sQuery(id+"F0.wireOp",EDGE,"E6.7.0.6"),sQuery(id+"F0.wireOp",EDGE,"E6.7.0.7"),sQuery(id+"F0.wireOp",EDGE,"E6.7.0.8"),sQuery(id+"F0.wireOp",EDGE,"E6.7.0.9"),sQuery(id+"F0.wireOp",EDGE,"E6.7.0.10"),sQuery(id+"F0.wireOp",EDGE,"E6.7.0.11"),sQuery(id+"F0.wireOp",EDGE,"E6.7.1.0"),sQuery(id+"F0.wireOp",EDGE,"E6.7.1.1"),sQuery(id+"F0.wireOp",EDGE,"E6.7.1.2"),sQuery(id+"F0.wireOp",EDGE,"E6.7.1.3"),sQuery(id+"F0.wireOp",EDGE,"E6.7.1.4"),sQuery(id+"F0.wireOp",EDGE,"E6.7.1.5"),sQuery(id+"F0.wireOp",EDGE,"E6.7.1.6"),sQuery(id+"F0.wireOp",EDGE,"E6.7.1.7"),sQuery(id+"F0.wireOp",EDGE,"E6.7.1.8"),sQuery(id+"F0.wireOp",EDGE,"E6.7.1.9"),sQuery(id+"F0.wireOp",EDGE,"E6.7.1.10"),sQuery(id+"F0.wireOp",EDGE,"E6.7.1.11"),sQuery(id+"F0.wireOp",EDGE,"E6.7.2.0"),sQuery(id+"F0.wireOp",EDGE,"E6.7.2.1"),sQuery(id+"F0.wireOp",EDGE,"E6.7.2.2"),sQuery(id+"F0.wireOp",EDGE,"E6.7.2.3"),sQuery(id+"F0.wireOp",EDGE,"E6.7.2.4"),sQuery(id+"F0.wireOp",EDGE,"E6.7.2.5"),sQuery(id+"F0.wireOp",EDGE,"E6.7.2.6"),sQuery(id+"F0.wireOp",EDGE,"E6.7.2.7"),sQuery(id+"F0.wireOp",EDGE,"E6.7.2.8"),sQuery(id+"F0.wireOp",EDGE,"E6.7.2.9"),sQuery(id+"F0.wireOp",EDGE,"E6.7.2.10"),sQuery(id+"F0.wireOp",EDGE,"E6.7.2.11"),sQuery(id+"F0.wireOp",EDGE,"E6.7.3.0"),sQuery(id+"F0.wireOp",EDGE,"E6.7.3.1"),sQuery(id+"F0.wireOp",EDGE,"E6.7.3.2"),sQuery(id+"F0.wireOp",EDGE,"E6.7.3.5"),sQuery(id+"F0.wireOp",EDGE,"E6.8.0.0"),sQuery(id+"F0.wireOp",EDGE,"E6.8.0.2"),sQuery(id+"F0.wireOp",EDGE,"E6.8.0.3"),sQuery(id+"F0.wireOp",EDGE,"E6.8.0.4"),sQuery(id+"F0.wireOp",EDGE,"E6.8.0.5"),sQuery(id+"F0.wireOp",EDGE,"E6.8.0.6"),sQuery(id+"F0.wireOp",EDGE,"E6.8.0.7"),sQuery(id+"F0.wireOp",EDGE,"E6.8.0.8"),sQuery(id+"F0.wireOp",EDGE,"E6.8.0.9"),sQuery(id+"F0.wireOp",EDGE,"E6.8.0.10"),sQuery(id+"F0.wireOp",EDGE,"E6.8.0.11"),sQuery(id+"F0.wireOp",EDGE,"E6.8.1.0"),sQuery(id+"F0.wireOp",EDGE,"E6.8.1.1"),sQuery(id+"F0.wireOp",EDGE,"E6.8.1.2"),sQuery(id+"F0.wireOp",EDGE,"E6.8.1.3"),sQuery(id+"F0.wireOp",EDGE,"E6.8.1.4"),sQuery(id+"F0.wireOp",EDGE,"E6.8.1.5"),sQuery(id+"F0.wireOp",EDGE,"E6.8.1.6"),sQuery(id+"F0.wireOp",EDGE,"E6.8.1.7"),sQuery(id+"F0.wireOp",EDGE,"E6.8.1.8"),sQuery(id+"F0.wireOp",EDGE,"E6.8.1.9"),sQuery(id+"F0.wireOp",EDGE,"E6.8.1.10"),sQuery(id+"F0.wireOp",EDGE,"E6.8.1.11"),sQuery(id+"F0.wireOp",EDGE,"E6.8.2.0"),sQuery(id+"F0.wireOp",EDGE,"E6.8.2.1"),sQuery(id+"F0.wireOp",EDGE,"E6.8.2.2"),sQuery(id+"F0.wireOp",EDGE,"E6.8.2.3"),sQuery(id+"F0.wireOp",EDGE,"E6.8.2.4"),sQuery(id+"F0.wireOp",EDGE,"E6.8.2.5"),sQuery(id+"F0.wireOp",EDGE,"E6.8.2.6"),sQuery(id+"F0.wireOp",EDGE,"E6.8.2.7"),sQuery(id+"F0.wireOp",EDGE,"E6.8.2.8"),sQuery(id+"F0.wireOp",EDGE,"E6.8.2.9"),sQuery(id+"F0.wireOp",EDGE,"E6.8.2.10"),sQuery(id+"F0.wireOp",EDGE,"E6.8.2.11"),sQuery(id+"F0.wireOp",EDGE,"E6.8.3.0"),sQuery(id+"F0.wireOp",EDGE,"E6.8.3.1"),sQuery(id+"F0.wireOp",EDGE,"E6.9.0.6"),sQuery(id+"F0.wireOp",EDGE,"E6.9.0.7"),sQuery(id+"F0.wireOp",EDGE,"E6.9.0.8"),sQuery(id+"F0.wireOp",EDGE,"E6.9.0.9"),sQuery(id+"F0.wireOp",EDGE,"E6.9.0.10"),sQuery(id+"F0.wireOp",EDGE,"E6.9.0.11"),sQuery(id+"F0.wireOp",EDGE,"E6.9.1.0"),sQuery(id+"F0.wireOp",EDGE,"E6.9.1.1"),sQuery(id+"F0.wireOp",EDGE,"E6.9.1.2"),sQuery(id+"F0.wireOp",EDGE,"E6.9.1.3"),sQuery(id+"F0.wireOp",EDGE,"E6.9.1.4"),sQuery(id+"F0.wireOp",EDGE,"E6.9.1.5"),sQuery(id+"F0.wireOp",EDGE,"E6.9.1.6"),sQuery(id+"F0.wireOp",EDGE,"E6.9.1.7"),sQuery(id+"F0.wireOp",EDGE,"E6.9.1.8"),sQuery(id+"F0.wireOp",EDGE,"E6.9.1.9"),sQuery(id+"F0.wireOp",EDGE,"E6.9.1.10"),sQuery(id+"F0.wireOp",EDGE,"E6.9.1.11"),sQuery(id+"F0.wireOp",EDGE,"E6.9.2.0"),sQuery(id+"F0.wireOp",EDGE,"E6.9.2.1"),sQuery(id+"F0.wireOp",EDGE,"E6.9.2.2"),sQuery(id+"F0.wireOp",EDGE,"E6.9.2.3"),sQuery(id+"F0.wireOp",EDGE,"E6.9.2.4"),sQuery(id+"F0.wireOp",EDGE,"E6.9.2.5"),sQuery(id+"F0.wireOp",EDGE,"E6.9.2.6"),sQuery(id+"F0.wireOp",EDGE,"E6.9.2.7"),sQuery(id+"F0.wireOp",EDGE,"E6.9.2.8"),sQuery(id+"F0.wireOp",EDGE,"E6.9.2.10"),sQuery(id+"F0.wireOp",EDGE,"E6.9.2.11"),sQuery(id+"F0.wireOp",EDGE,"E6.10.0.6"),sQuery(id+"F0.wireOp",EDGE,"E6.10.0.10"),sQuery(id+"F0.wireOp",EDGE,"E6.10.0.11"),sQuery(id+"F0.wireOp",EDGE,"E6.10.1.0"),sQuery(id+"F0.wireOp",EDGE,"E6.10.1.4"),sQuery(id+"F0.wireOp",EDGE,"E6.10.1.5"),sQuery(id+"F0.wireOp",EDGE,"E6.10.1.6"),sQuery(id+"F0.wireOp",EDGE,"E6.10.1.7"),sQuery(id+"F0.wireOp",EDGE,"E6.10.1.9"),sQuery(id+"F0.wireOp",EDGE,"E6.10.1.10"),sQuery(id+"F0.wireOp",EDGE,"E6.10.1.11"),sQuery(id+"F0.wireOp",EDGE,"E6.10.2.0"),sQuery(id+"F0.wireOp",EDGE,"E6.10.2.5"),sQuery(id+"F0.wireOp",EDGE,"E7.trimOffspring"),sQuery(id+"F0.wireOp",EDGE,"E9"),sQuery(id+"F0.wireOp",EDGE,"E12.trimOffspring"),sQuery(id+"F0.wireOp",EDGE,"E13"),sQuery(id+"F0.wireOp",EDGE,"E14.trimOffspring"),sQuery(id+"F0.wireOp",EDGE,"E17"),sQuery(id+"F0.wireOp",EDGE,"E18.trimOffspring"),sQuery(id+"F0.wireOp",EDGE,"E26.trimOffspring"),sQuery(id+"F0.wireOp",EDGE,"E27.trimOffspring"),sQuery(id+"F0.wireOp",EDGE,"E28.trimOffspring"),sQuery(id+"F0.wireOp",EDGE,"E34"),sQuery(id+"F0.wireOp",EDGE,"E35"),sQuery(id+"F0.wireOp",EDGE,"E36"),sQuery(id+"F0.wireOp",EDGE,"E37"),sQuery(id+"F0.wireOp",EDGE,"E38"),sQuery(id+"F0.wireOp",EDGE,"E39"),sQuery(id+"F0.wireOp",EDGE,"E40"),sQuery(id+"F0.wireOp",EDGE,"E41"),sQuery(id+"F0.wireOp",EDGE,"E42"),sQuery(id+"F0.wireOp",EDGE,"E43"),sQuery(id+"F0.wireOp",EDGE,"E44"),sQuery(id+"F0.wireOp",EDGE,"E45"),sQuery(id+"F0.wireOp",EDGE,"E46"),sQuery(id+"F0.wireOp",EDGE,"E47"),sQuery(id+"F0.wireOp",EDGE,"E48"),sQuery(id+"F0.wireOp",EDGE,"E49")])],"isStart":false});
            extrude(context, id + "F2", {"entities" : qUnion([Q0]), "depth" : 1.5 * mm});
        }
        {
            var Q0;
            Q0=makeQuery(id+"F2.opExtrude","SWEPT_EDGE",EDGE,{"disambiguationData":[OSD([sQuery(id+"F0.wireOp",EDGE,"E6.5.0.1"),sQuery(id+"F0.wireOp",EDGE,"E9")])]});
            var Q1;
            Q1=makeQuery(id+"F2.opExtrude","SWEPT_EDGE",EDGE,{"disambiguationData":[OSD([sQuery(id+"F0.wireOp",EDGE,"E6.5.0.1"),sQuery(id+"F0.wireOp",EDGE,"E6.5.0.2")])]});
            var Q2;
            Q2=makeQuery(id+"F2.opExtrude","SWEPT_EDGE",EDGE,{"disambiguationData":[OSD([sQuery(id+"F0.wireOp",EDGE,"E6.5.0.0"),sQuery(id+"F0.wireOp",EDGE,"E9")])]});
            var Q3;
            Q3=makeQuery(id+"F2.opExtrude","SWEPT_EDGE",EDGE,{"disambiguationData":[OSD([sQuery(id+"F0.wireOp",EDGE,"E6.8.0.6"),sQuery(id+"F0.wireOp",EDGE,"E6.8.0.7")])]});
            var Q4;
            Q4=makeQuery(id+"F2.opExtrude","SWEPT_EDGE",EDGE,{"disambiguationData":[OSD([sQuery(id+"F0.wireOp",EDGE,"E6.8.0.2"),sQuery(id+"F0.wireOp",EDGE,"E38")])]});
            var Q5;
            Q5=makeQuery(id+"F2.opExtrude","SWEPT_EDGE",EDGE,{"disambiguationData":[OSD([sQuery(id+"F0.wireOp",EDGE,"E6.9.0.7"),sQuery(id+"F0.wireOp",EDGE,"E6.9.0.8")])]});
            var Q6;
            Q6=makeQuery(id+"F2.opExtrude","SWEPT_EDGE",EDGE,{"disambiguationData":[OSD([sQuery(id+"F0.wireOp",EDGE,"E6.9.1.0"),sQuery(id+"F0.wireOp",EDGE,"E6.9.1.1")])]});
            var Q7;
            Q7=makeQuery(id+"F2.opExtrude","SWEPT_EDGE",EDGE,{"disambiguationData":[OSD([sQuery(id+"F0.wireOp",EDGE,"E6.7.0.6"),sQuery(id+"F0.wireOp",EDGE,"E6.7.0.7")])]});
            var Q8;
            Q8=makeQuery(id+"F2.opExtrude","SWEPT_EDGE",EDGE,{"disambiguationData":[OSD([sQuery(id+"F0.wireOp",EDGE,"E6.7.1.1"),sQuery(id+"F0.wireOp",EDGE,"E6.7.1.2")])]});
            var Q9;
            Q9=makeQuery(id+"F2.opExtrude","SWEPT_EDGE",EDGE,{"disambiguationData":[OSD([sQuery(id+"F0.wireOp",EDGE,"E6.8.1.1"),sQuery(id+"F0.wireOp",EDGE,"E6.8.1.2")])]});
            var Q10;
            Q10=makeQuery(id+"F2.opExtrude","SWEPT_EDGE",EDGE,{"disambiguationData":[OSD([sQuery(id+"F0.wireOp",EDGE,"E6.10.1.7"),sQuery(id+"F0.wireOp",EDGE,"E48")])]});
            var Q11;
            Q11=makeQuery(id+"F2.opExtrude","SWEPT_EDGE",EDGE,{"disambiguationData":[OSD([sQuery(id+"F0.wireOp",EDGE,"E6.6.0.10"),sQuery(id+"F0.wireOp",EDGE,"E6.6.0.11")])]});
            var Q12;
            Q12=makeQuery(id+"F2.opExtrude","SWEPT_EDGE",EDGE,{"disambiguationData":[OSD([sQuery(id+"F0.wireOp",EDGE,"E6.5.0.6"),sQuery(id+"F0.wireOp",EDGE,"E6.5.0.11")])]});
            var Q13;
            Q13=makeQuery(id+"F2.opExtrude","SWEPT_EDGE",EDGE,{"disambiguationData":[OSD([sQuery(id+"F0.wireOp",EDGE,"E6.4.0.8"),sQuery(id+"F0.wireOp",EDGE,"E6.4.0.9")])]});
            var Q14;
            Q14=makeQuery(id+"F2.opExtrude","SWEPT_EDGE",EDGE,{"disambiguationData":[OSD([sQuery(id+"F0.wireOp",EDGE,"E6.4.1.1"),sQuery(id+"F0.wireOp",EDGE,"E6.4.1.2")])]});
            var Q15;
            Q15=makeQuery(id+"F2.opExtrude","SWEPT_EDGE",EDGE,{"disambiguationData":[OSD([sQuery(id+"F0.wireOp",EDGE,"E6.5.1.1"),sQuery(id+"F0.wireOp",EDGE,"E6.5.1.2")])]});
            var Q16;
            Q16=makeQuery(id+"F2.opExtrude","SWEPT_EDGE",EDGE,{"disambiguationData":[OSD([sQuery(id+"F0.wireOp",EDGE,"E6.6.1.0"),sQuery(id+"F0.wireOp",EDGE,"E6.6.1.5")])]});
            var Q17;
            Q17=makeQuery(id+"F2.opExtrude","SWEPT_EDGE",EDGE,{"disambiguationData":[OSD([sQuery(id+"F0.wireOp",EDGE,"E6.6.1.6"),sQuery(id+"F0.wireOp",EDGE,"E6.6.1.11")])]});
            var Q18;
            Q18=makeQuery(id+"F2.opExtrude","SWEPT_EDGE",EDGE,{"disambiguationData":[OSD([sQuery(id+"F0.wireOp",EDGE,"E6.5.1.6"),sQuery(id+"F0.wireOp",EDGE,"E6.5.1.7")])]});
            var Q19;
            Q19=makeQuery(id+"F2.opExtrude","SWEPT_EDGE",EDGE,{"disambiguationData":[OSD([sQuery(id+"F0.wireOp",EDGE,"E6.4.1.6"),sQuery(id+"F0.wireOp",EDGE,"E6.4.1.11")])]});
            var Q20;
            Q20=makeQuery(id+"F2.opExtrude","SWEPT_EDGE",EDGE,{"disambiguationData":[OSD([sQuery(id+"F0.wireOp",EDGE,"E6.3.1.0"),sQuery(id+"F0.wireOp",EDGE,"E6.3.1.5")])]});
            var Q21;
            Q21=makeQuery(id+"F2.opExtrude","SWEPT_EDGE",EDGE,{"disambiguationData":[OSD([sQuery(id+"F0.wireOp",EDGE,"E6.3.1.6"),sQuery(id+"F0.wireOp",EDGE,"E6.3.1.11")])]});
            var Q22;
            Q22=makeQuery(id+"F2.opExtrude","SWEPT_EDGE",EDGE,{"disambiguationData":[OSD([sQuery(id+"F0.wireOp",EDGE,"E6.3.2.0"),sQuery(id+"F0.wireOp",EDGE,"E6.3.2.1")])]});
            var Q23;
            Q23=makeQuery(id+"F2.opExtrude","SWEPT_EDGE",EDGE,{"disambiguationData":[OSD([sQuery(id+"F0.wireOp",EDGE,"E6.4.2.4"),sQuery(id+"F0.wireOp",EDGE,"E6.4.2.5")])]});
            var Q24;
            Q24=makeQuery(id+"F2.opExtrude","SWEPT_EDGE",EDGE,{"disambiguationData":[OSD([sQuery(id+"F0.wireOp",EDGE,"E6.5.2.0"),sQuery(id+"F0.wireOp",EDGE,"E6.5.2.5")])]});
            var Q25;
            Q25=makeQuery(id+"F2.opExtrude","SWEPT_EDGE",EDGE,{"disambiguationData":[OSD([sQuery(id+"F0.wireOp",EDGE,"E6.4.2.11"),sQuery(id+"F0.wireOp",EDGE,"E40")])]});
            var Q26;
            Q26=makeQuery(id+"F2.opExtrude","SWEPT_EDGE",EDGE,{"disambiguationData":[OSD([sQuery(id+"F0.wireOp",EDGE,"E6.7.1.6"),sQuery(id+"F0.wireOp",EDGE,"E6.7.1.7")])]});
            var Q27;
            Q27=makeQuery(id+"F2.opExtrude","SWEPT_EDGE",EDGE,{"disambiguationData":[OSD([sQuery(id+"F0.wireOp",EDGE,"E6.8.1.6"),sQuery(id+"F0.wireOp",EDGE,"E6.8.1.11")])]});
            var Q28;
            Q28=makeQuery(id+"F2.opExtrude","SWEPT_EDGE",EDGE,{"disambiguationData":[OSD([sQuery(id+"F0.wireOp",EDGE,"E6.9.1.6"),sQuery(id+"F0.wireOp",EDGE,"E6.9.1.11")])]});
            var Q29;
            Q29=makeQuery(id+"F2.opExtrude","SWEPT_EDGE",EDGE,{"disambiguationData":[OSD([sQuery(id+"F0.wireOp",EDGE,"E6.8.2.0"),sQuery(id+"F0.wireOp",EDGE,"E6.8.2.5")])]});
            var Q30;
            Q30=makeQuery(id+"F2.opExtrude","SWEPT_EDGE",EDGE,{"disambiguationData":[OSD([sQuery(id+"F0.wireOp",EDGE,"E6.7.2.2"),sQuery(id+"F0.wireOp",EDGE,"E6.7.2.3")])]});
            var Q31;
            Q31=makeQuery(id+"F2.opExtrude","SWEPT_EDGE",EDGE,{"disambiguationData":[OSD([sQuery(id+"F0.wireOp",EDGE,"E6.9.2.2"),sQuery(id+"F0.wireOp",EDGE,"E6.9.2.3")])]});
            var Q32;
            Q32=makeQuery(id+"F2.opExtrude","SWEPT_EDGE",EDGE,{"disambiguationData":[OSD([sQuery(id+"F0.wireOp",EDGE,"E6.6.2.2"),sQuery(id+"F0.wireOp",EDGE,"E6.6.2.3")])]});
            var Q33;
            Q33=makeQuery(id+"F2.opExtrude","SWEPT_EDGE",EDGE,{"disambiguationData":[OSD([sQuery(id+"F0.wireOp",EDGE,"E6.5.2.7"),sQuery(id+"F0.wireOp",EDGE,"E6.5.2.8")])]});
            var Q34;
            Q34=makeQuery(id+"F2.opExtrude","SWEPT_EDGE",EDGE,{"disambiguationData":[OSD([sQuery(id+"F0.wireOp",EDGE,"E6.6.2.8"),sQuery(id+"F0.wireOp",EDGE,"E6.6.2.9")])]});
            var Q35;
            Q35=makeQuery(id+"F2.opExtrude","SWEPT_EDGE",EDGE,{"disambiguationData":[OSD([sQuery(id+"F0.wireOp",EDGE,"E6.7.2.6"),sQuery(id+"F0.wireOp",EDGE,"E6.7.2.11")])]});
            var Q36;
            Q36=makeQuery(id+"F2.opExtrude","SWEPT_EDGE",EDGE,{"disambiguationData":[OSD([sQuery(id+"F0.wireOp",EDGE,"E6.8.2.6"),sQuery(id+"F0.wireOp",EDGE,"E6.8.2.11")])]});
            var Q37;
            Q37=makeQuery(id+"F2.opExtrude","SWEPT_EDGE",EDGE,{"disambiguationData":[OSD([sQuery(id+"F0.wireOp",EDGE,"E6.9.2.6"),sQuery(id+"F0.wireOp",EDGE,"E6.9.2.11")])]});
            var Q38;
            Q38=makeQuery(id+"F2.opExtrude","SWEPT_EDGE",EDGE,{"disambiguationData":[OSD([sQuery(id+"F0.wireOp",EDGE,"E6.7.3.0"),sQuery(id+"F0.wireOp",EDGE,"E6.7.3.1")])]});
            var Q39;
            Q39=makeQuery(id+"F2.opExtrude","SWEPT_EDGE",EDGE,{"disambiguationData":[OSD([sQuery(id+"F0.wireOp",EDGE,"E6.6.3.0"),sQuery(id+"F0.wireOp",EDGE,"E6.6.3.5")])]});
            var Q40;
            Q40=makeQuery(id+"F2.opExtrude","SWEPT_EDGE",EDGE,{"disambiguationData":[OSD([sQuery(id+"F0.wireOp",EDGE,"E6.4.3.1"),sQuery(id+"F0.wireOp",EDGE,"E26.trimOffspring")])]});
            fillet(context, id + "F3", {"entities" : qUnion([Q0, Q1, Q2, Q3, Q4, Q5, Q6, Q7, Q8, Q9, Q10, Q11, Q12, Q13, Q14, Q15, Q16, Q17, Q18, Q19, Q20, Q21, Q22, Q23, Q24, Q25, Q26, Q27, Q28, Q29, Q30, Q31, Q32, Q33, Q34, Q35, Q36, Q37, Q38, Q39, Q40]), "radius" : 5 * mm, "tangentPropagation" : true, "allowEdgeOverflow" : false});
        }
        {
            var Q0;
            Q0=makeQuery(id+"F2.opExtrude","SWEPT_EDGE",EDGE,{"disambiguationData":[OSD([sQuery(id+"F0.wireOp",EDGE,"E6.6.0.0"),sQuery(id+"F0.wireOp",EDGE,"E6.6.0.1")])]});
            var Q1;
            Q1=makeQuery(id+"F2.opExtrude","SWEPT_EDGE",EDGE,{"disambiguationData":[OSD([sQuery(id+"F0.wireOp",EDGE,"E6.5.0.0"),sQuery(id+"F0.wireOp",EDGE,"E6.5.0.5")])]});
            var Q2;
            Q2=makeQuery(id+"F2.opExtrude","SWEPT_EDGE",EDGE,{"disambiguationData":[OSD([sQuery(id+"F0.wireOp",EDGE,"E6.9.0.6"),sQuery(id+"F0.wireOp",EDGE,"E6.9.0.7")])]});
            var Q3;
            Q3=makeQuery(id+"F2.opExtrude","SWEPT_EDGE",EDGE,{"disambiguationData":[OSD([sQuery(id+"F0.wireOp",EDGE,"E6.8.0.6"),sQuery(id+"F0.wireOp",EDGE,"E6.8.0.11")])]});
            var Q4;
            Q4=makeQuery(id+"F2.opExtrude","SWEPT_EDGE",EDGE,{"disambiguationData":[OSD([sQuery(id+"F0.wireOp",EDGE,"E6.6.0.7"),sQuery(id+"F0.wireOp",EDGE,"E6.6.0.8")])]});
            var Q5;
            Q5=makeQuery(id+"F2.opExtrude","SWEPT_EDGE",EDGE,{"disambiguationData":[OSD([sQuery(id+"F0.wireOp",EDGE,"E6.7.0.9"),sQuery(id+"F0.wireOp",EDGE,"E6.7.0.10")])]});
            var Q6;
            Q6=makeQuery(id+"F2.opExtrude","SWEPT_EDGE",EDGE,{"disambiguationData":[OSD([sQuery(id+"F0.wireOp",EDGE,"E6.8.0.9"),sQuery(id+"F0.wireOp",EDGE,"E6.8.0.10")])]});
            var Q7;
            Q7=makeQuery(id+"F2.opExtrude","SWEPT_EDGE",EDGE,{"disambiguationData":[OSD([sQuery(id+"F0.wireOp",EDGE,"E6.9.0.10"),sQuery(id+"F0.wireOp",EDGE,"E6.9.0.11")])]});
            var Q8;
            Q8=makeQuery(id+"F2.opExtrude","SWEPT_EDGE",EDGE,{"disambiguationData":[OSD([sQuery(id+"F0.wireOp",EDGE,"E6.8.1.4"),sQuery(id+"F0.wireOp",EDGE,"E6.8.1.5")])]});
            var Q9;
            Q9=makeQuery(id+"F2.opExtrude","SWEPT_EDGE",EDGE,{"disambiguationData":[OSD([sQuery(id+"F0.wireOp",EDGE,"E6.7.1.4"),sQuery(id+"F0.wireOp",EDGE,"E6.7.1.5")])]});
            var Q10;
            Q10=makeQuery(id+"F2.opExtrude","SWEPT_EDGE",EDGE,{"disambiguationData":[OSD([sQuery(id+"F0.wireOp",EDGE,"E6.6.1.2"),sQuery(id+"F0.wireOp",EDGE,"E6.6.1.3")])]});
            var Q11;
            Q11=makeQuery(id+"F2.opExtrude","SWEPT_EDGE",EDGE,{"disambiguationData":[OSD([sQuery(id+"F0.wireOp",EDGE,"E6.5.1.4"),sQuery(id+"F0.wireOp",EDGE,"E6.5.1.5")])]});
            var Q12;
            Q12=makeQuery(id+"F2.opExtrude","SWEPT_EDGE",EDGE,{"disambiguationData":[OSD([sQuery(id+"F0.wireOp",EDGE,"E6.6.1.8"),sQuery(id+"F0.wireOp",EDGE,"E6.6.1.9")])]});
            var Q13;
            Q13=makeQuery(id+"F2.opExtrude","SWEPT_EDGE",EDGE,{"disambiguationData":[OSD([sQuery(id+"F0.wireOp",EDGE,"E6.7.1.9"),sQuery(id+"F0.wireOp",EDGE,"E6.7.1.10")])]});
            var Q14;
            Q14=makeQuery(id+"F2.opExtrude","SWEPT_EDGE",EDGE,{"disambiguationData":[OSD([sQuery(id+"F0.wireOp",EDGE,"E6.8.1.8"),sQuery(id+"F0.wireOp",EDGE,"E6.8.1.9")])]});
            var Q15;
            Q15=makeQuery(id+"F2.opExtrude","SWEPT_EDGE",EDGE,{"disambiguationData":[OSD([sQuery(id+"F0.wireOp",EDGE,"E6.9.1.8"),sQuery(id+"F0.wireOp",EDGE,"E6.9.1.9")])]});
            var Q16;
            Q16=makeQuery(id+"F2.opExtrude","SWEPT_EDGE",EDGE,{"disambiguationData":[OSD([sQuery(id+"F0.wireOp",EDGE,"E6.10.1.10"),sQuery(id+"F0.wireOp",EDGE,"E6.10.1.11")])]});
            var Q17;
            Q17=makeQuery(id+"F2.opExtrude","SWEPT_EDGE",EDGE,{"disambiguationData":[OSD([sQuery(id+"F0.wireOp",EDGE,"E6.9.2.0"),sQuery(id+"F0.wireOp",EDGE,"E6.9.2.5")])]});
            var Q18;
            Q18=makeQuery(id+"F2.opExtrude","SWEPT_EDGE",EDGE,{"disambiguationData":[OSD([sQuery(id+"F0.wireOp",EDGE,"E6.10.2.0"),sQuery(id+"F0.wireOp",EDGE,"E6.10.2.5")])]});
            var Q19;
            Q19=makeQuery(id+"F2.opExtrude","SWEPT_EDGE",EDGE,{"disambiguationData":[OSD([sQuery(id+"F0.wireOp",EDGE,"E6.7.2.0"),sQuery(id+"F0.wireOp",EDGE,"E6.7.2.5")])]});
            var Q20;
            Q20=makeQuery(id+"F2.opExtrude","SWEPT_EDGE",EDGE,{"disambiguationData":[OSD([sQuery(id+"F0.wireOp",EDGE,"E6.8.2.8"),sQuery(id+"F0.wireOp",EDGE,"E6.8.2.9")])]});
            var Q21;
            Q21=makeQuery(id+"F2.opExtrude","SWEPT_EDGE",EDGE,{"disambiguationData":[OSD([sQuery(id+"F0.wireOp",EDGE,"E6.5.0.3"),sQuery(id+"F0.wireOp",EDGE,"E6.5.0.4")])]});
            var Q22;
            Q22=makeQuery(id+"F2.opExtrude","SWEPT_EDGE",EDGE,{"disambiguationData":[OSD([sQuery(id+"F0.wireOp",EDGE,"E6.7.0.3"),sQuery(id+"F0.wireOp",EDGE,"E6.7.0.4")])]});
            var Q23;
            Q23=makeQuery(id+"F2.opExtrude","SWEPT_EDGE",EDGE,{"disambiguationData":[OSD([sQuery(id+"F0.wireOp",EDGE,"E6.5.0.8"),sQuery(id+"F0.wireOp",EDGE,"E6.5.0.9")])]});
            var Q24;
            Q24=makeQuery(id+"F2.opExtrude","SWEPT_EDGE",EDGE,{"disambiguationData":[OSD([sQuery(id+"F0.wireOp",EDGE,"E6.4.0.2"),sQuery(id+"F0.wireOp",EDGE,"E6.4.0.3")])]});
            var Q25;
            Q25=makeQuery(id+"F2.opExtrude","SWEPT_EDGE",EDGE,{"disambiguationData":[OSD([sQuery(id+"F0.wireOp",EDGE,"E6.4.0.3"),sQuery(id+"F0.wireOp",EDGE,"E6.4.0.4")])]});
            var Q26;
            Q26=makeQuery(id+"F2.opExtrude","SWEPT_EDGE",EDGE,{"disambiguationData":[OSD([sQuery(id+"F0.wireOp",EDGE,"E6.6.2.0"),sQuery(id+"F0.wireOp",EDGE,"E6.6.2.5")])]});
            var Q27;
            Q27=makeQuery(id+"F2.opExtrude","SWEPT_EDGE",EDGE,{"disambiguationData":[OSD([sQuery(id+"F0.wireOp",EDGE,"E6.7.2.8"),sQuery(id+"F0.wireOp",EDGE,"E6.7.2.9")])]});
            var Q28;
            Q28=makeQuery(id+"F2.opExtrude","SWEPT_EDGE",EDGE,{"disambiguationData":[OSD([sQuery(id+"F0.wireOp",EDGE,"E6.6.3.1"),sQuery(id+"F0.wireOp",EDGE,"E6.6.3.2")])]});
            var Q29;
            Q29=makeQuery(id+"F2.opExtrude","SWEPT_EDGE",EDGE,{"disambiguationData":[OSD([sQuery(id+"F0.wireOp",EDGE,"E6.6.2.6"),sQuery(id+"F0.wireOp",EDGE,"E6.6.2.11")])]});
            var Q30;
            Q30=makeQuery(id+"F2.opExtrude","SWEPT_EDGE",EDGE,{"disambiguationData":[OSD([sQuery(id+"F0.wireOp",EDGE,"E6.5.2.1"),sQuery(id+"F0.wireOp",EDGE,"E6.5.2.2")])]});
            var Q31;
            Q31=makeQuery(id+"F2.opExtrude","SWEPT_EDGE",EDGE,{"disambiguationData":[OSD([sQuery(id+"F0.wireOp",EDGE,"E6.5.1.9"),sQuery(id+"F0.wireOp",EDGE,"E6.5.1.10")])]});
            var Q32;
            Q32=makeQuery(id+"F2.opExtrude","SWEPT_EDGE",EDGE,{"disambiguationData":[OSD([sQuery(id+"F0.wireOp",EDGE,"E6.4.1.4"),sQuery(id+"F0.wireOp",EDGE,"E6.4.1.5")])]});
            var Q33;
            Q33=makeQuery(id+"F2.opExtrude","SWEPT_EDGE",EDGE,{"disambiguationData":[OSD([sQuery(id+"F0.wireOp",EDGE,"E6.4.1.8"),sQuery(id+"F0.wireOp",EDGE,"E6.4.1.9")])]});
            var Q34;
            Q34=makeQuery(id+"F2.opExtrude","SWEPT_EDGE",EDGE,{"disambiguationData":[OSD([sQuery(id+"F0.wireOp",EDGE,"E6.4.2.1"),sQuery(id+"F0.wireOp",EDGE,"E6.4.2.2")])]});
            var Q35;
            Q35=makeQuery(id+"F2.opExtrude","SWEPT_EDGE",EDGE,{"disambiguationData":[OSD([sQuery(id+"F0.wireOp",EDGE,"E6.3.1.2"),sQuery(id+"F0.wireOp",EDGE,"E6.3.1.3")])]});
            var Q36;
            Q36=makeQuery(id+"F2.opExtrude","SWEPT_EDGE",EDGE,{"disambiguationData":[OSD([sQuery(id+"F0.wireOp",EDGE,"E6.5.2.10"),sQuery(id+"F0.wireOp",EDGE,"E6.5.2.11")])]});
            var Q37;
            Q37=makeQuery(id+"F2.opExtrude","SWEPT_EDGE",EDGE,{"disambiguationData":[OSD([sQuery(id+"F0.wireOp",EDGE,"E6.4.0.6"),sQuery(id+"F0.wireOp",EDGE,"E6.4.0.11")])]});
            var Q38;
            Q38=makeQuery(id+"F2.opExtrude","SWEPT_EDGE",EDGE,{"disambiguationData":[OSD([sQuery(id+"F0.wireOp",EDGE,"E6.3.1.8"),sQuery(id+"F0.wireOp",EDGE,"E6.3.1.9")])]});
            var Q39;
            Q39=makeQuery(id+"F2.opExtrude","SWEPT_EDGE",EDGE,{"disambiguationData":[OSD([sQuery(id+"F0.wireOp",EDGE,"E6.3.2.2"),sQuery(id+"F0.wireOp",EDGE,"E6.3.2.3")])]});
            var Q40;
            Q40=makeQuery(id+"F2.opExtrude","SWEPT_EDGE",EDGE,{"disambiguationData":[OSD([sQuery(id+"F0.wireOp",EDGE,"E6.3.2.4"),sQuery(id+"F0.wireOp",EDGE,"E6.3.2.5")])]});
            var Q41;
            Q41=makeQuery(id+"F2.opExtrude","SWEPT_EDGE",EDGE,{"disambiguationData":[OSD([sQuery(id+"F0.wireOp",EDGE,"E6.3.2.3"),sQuery(id+"F0.wireOp",EDGE,"E6.3.2.4")])]});
            var Q42;
            Q42=makeQuery(id+"F2.opExtrude","SWEPT_EDGE",EDGE,{"disambiguationData":[OSD([sQuery(id+"F0.wireOp",EDGE,"E6.6.0.3"),sQuery(id+"F0.wireOp",EDGE,"E6.6.0.4")])]});
            var Q43;
            Q43=makeQuery(id+"F2.opExtrude","SWEPT_EDGE",EDGE,{"disambiguationData":[OSD([sQuery(id+"F0.wireOp",EDGE,"E6.6.0.2"),sQuery(id+"F0.wireOp",EDGE,"E6.6.0.3")])]});
            var Q44;
            Q44=makeQuery(id+"F2.opExtrude","SWEPT_EDGE",EDGE,{"disambiguationData":[OSD([sQuery(id+"F0.wireOp",EDGE,"E6.7.0.1"),sQuery(id+"F0.wireOp",EDGE,"E37")])]});
            var Q45;
            Q45=makeQuery(id+"F2.opExtrude","SWEPT_EDGE",EDGE,{"disambiguationData":[OSD([sQuery(id+"F0.wireOp",EDGE,"E6.7.0.0"),sQuery(id+"F0.wireOp",EDGE,"E37")])]});
            var Q46;
            Q46=makeQuery(id+"F2.opExtrude","SWEPT_EDGE",EDGE,{"disambiguationData":[OSD([sQuery(id+"F0.wireOp",EDGE,"E6.7.0.4"),sQuery(id+"F0.wireOp",EDGE,"E6.7.0.5")])]});
            var Q47;
            Q47=makeQuery(id+"F2.opExtrude","SWEPT_EDGE",EDGE,{"disambiguationData":[OSD([sQuery(id+"F0.wireOp",EDGE,"E6.7.0.2"),sQuery(id+"F0.wireOp",EDGE,"E6.7.0.3")])]});
            fillet(context, id + "F4", {"entities" : qUnion([Q0, Q1, Q2, Q3, Q4, Q5, Q6, Q7, Q8, Q9, Q10, Q11, Q12, Q13, Q14, Q15, Q16, Q17, Q18, Q19, Q20, Q21, Q22, Q23, Q24, Q25, Q26, Q27, Q28, Q29, Q30, Q31, Q32, Q33, Q34, Q35, Q36, Q37, Q38, Q39, Q40, Q41, Q42, Q43, Q44, Q45, Q46, Q47]), "radius" : 2 * mm, "tangentPropagation" : true, "allowEdgeOverflow" : false});
        }
        {
            var Q0;
            Q0=makeQuery(id+"F2.opExtrude","CAP_FACE",FACE,{"disambiguationData":[OSD([sQuery(id+"F0.wireOp",EDGE,"E0"),sQuery(id+"F0.wireOp",EDGE,"E6.2.1.2"),sQuery(id+"F0.wireOp",EDGE,"E6.2.1.3"),sQuery(id+"F0.wireOp",EDGE,"E6.3.0.8"),sQuery(id+"F0.wireOp",EDGE,"E6.3.0.9"),sQuery(id+"F0.wireOp",EDGE,"E6.3.0.10"),sQuery(id+"F0.wireOp",EDGE,"E6.3.1.0"),sQuery(id+"F0.wireOp",EDGE,"E6.3.1.1"),sQuery(id+"F0.wireOp",EDGE,"E6.3.1.2"),sQuery(id+"F0.wireOp",EDGE,"E6.3.1.3"),sQuery(id+"F0.wireOp",EDGE,"E6.3.1.4"),sQuery(id+"F0.wireOp",EDGE,"E6.3.1.5"),sQuery(id+"F0.wireOp",EDGE,"E6.3.1.6"),sQuery(id+"F0.wireOp",EDGE,"E6.3.1.7"),sQuery(id+"F0.wireOp",EDGE,"E6.3.1.8"),sQuery(id+"F0.wireOp",EDGE,"E6.3.1.9"),sQuery(id+"F0.wireOp",EDGE,"E6.3.1.10"),sQuery(id+"F0.wireOp",EDGE,"E6.3.1.11"),sQuery(id+"F0.wireOp",EDGE,"E6.3.2.0"),sQuery(id+"F0.wireOp",EDGE,"E6.3.2.1"),sQuery(id+"F0.wireOp",EDGE,"E6.3.2.2"),sQuery(id+"F0.wireOp",EDGE,"E6.3.2.3"),sQuery(id+"F0.wireOp",EDGE,"E6.3.2.4"),sQuery(id+"F0.wireOp",EDGE,"E6.3.2.5"),sQuery(id+"F0.wireOp",EDGE,"E6.4.0.2"),sQuery(id+"F0.wireOp",EDGE,"E6.4.0.3"),sQuery(id+"F0.wireOp",EDGE,"E6.4.0.4"),sQuery(id+"F0.wireOp",EDGE,"E6.4.0.5"),sQuery(id+"F0.wireOp",EDGE,"E6.4.0.6"),sQuery(id+"F0.wireOp",EDGE,"E6.4.0.7"),sQuery(id+"F0.wireOp",EDGE,"E6.4.0.8"),sQuery(id+"F0.wireOp",EDGE,"E6.4.0.9"),sQuery(id+"F0.wireOp",EDGE,"E6.4.0.10"),sQuery(id+"F0.wireOp",EDGE,"E6.4.0.11"),sQuery(id+"F0.wireOp",EDGE,"E6.4.1.0"),sQuery(id+"F0.wireOp",EDGE,"E6.4.1.1"),sQuery(id+"F0.wireOp",EDGE,"E6.4.1.2"),sQuery(id+"F0.wireOp",EDGE,"E6.4.1.3"),sQuery(id+"F0.wireOp",EDGE,"E6.4.1.4"),sQuery(id+"F0.wireOp",EDGE,"E6.4.1.5"),sQuery(id+"F0.wireOp",EDGE,"E6.4.1.6"),sQuery(id+"F0.wireOp",EDGE,"E6.4.1.7"),sQuery(id+"F0.wireOp",EDGE,"E6.4.1.8"),sQuery(id+"F0.wireOp",EDGE,"E6.4.1.9"),sQuery(id+"F0.wireOp",EDGE,"E6.4.1.10"),sQuery(id+"F0.wireOp",EDGE,"E6.4.1.11"),sQuery(id+"F0.wireOp",EDGE,"E6.4.2.0"),sQuery(id+"F0.wireOp",EDGE,"E6.4.2.1"),sQuery(id+"F0.wireOp",EDGE,"E6.4.2.2"),sQuery(id+"F0.wireOp",EDGE,"E6.4.2.3"),sQuery(id+"F0.wireOp",EDGE,"E6.4.2.4"),sQuery(id+"F0.wireOp",EDGE,"E6.4.2.5"),sQuery(id+"F0.wireOp",EDGE,"E6.4.2.6"),sQuery(id+"F0.wireOp",EDGE,"E6.4.2.7"),sQuery(id+"F0.wireOp",EDGE,"E6.4.2.8"),sQuery(id+"F0.wireOp",EDGE,"E6.4.2.9"),sQuery(id+"F0.wireOp",EDGE,"E6.4.2.11"),sQuery(id+"F0.wireOp",EDGE,"E6.4.3.1"),sQuery(id+"F0.wireOp",EDGE,"E6.4.3.2"),sQuery(id+"F0.wireOp",EDGE,"E6.5.0.0"),sQuery(id+"F0.wireOp",EDGE,"E6.5.0.1"),sQuery(id+"F0.wireOp",EDGE,"E6.5.0.2"),sQuery(id+"F0.wireOp",EDGE,"E6.5.0.3"),sQuery(id+"F0.wireOp",EDGE,"E6.5.0.4"),sQuery(id+"F0.wireOp",EDGE,"E6.5.0.5"),sQuery(id+"F0.wireOp",EDGE,"E6.5.0.6"),sQuery(id+"F0.wireOp",EDGE,"E6.5.0.7"),sQuery(id+"F0.wireOp",EDGE,"E6.5.0.8"),sQuery(id+"F0.wireOp",EDGE,"E6.5.0.9"),sQuery(id+"F0.wireOp",EDGE,"E6.5.0.10"),sQuery(id+"F0.wireOp",EDGE,"E6.5.0.11"),sQuery(id+"F0.wireOp",EDGE,"E6.5.1.0"),sQuery(id+"F0.wireOp",EDGE,"E6.5.1.1"),sQuery(id+"F0.wireOp",EDGE,"E6.5.1.2"),sQuery(id+"F0.wireOp",EDGE,"E6.5.1.3"),sQuery(id+"F0.wireOp",EDGE,"E6.5.1.4"),sQuery(id+"F0.wireOp",EDGE,"E6.5.1.5"),sQuery(id+"F0.wireOp",EDGE,"E6.5.1.6"),sQuery(id+"F0.wireOp",EDGE,"E6.5.1.7"),sQuery(id+"F0.wireOp",EDGE,"E6.5.1.8"),sQuery(id+"F0.wireOp",EDGE,"E6.5.1.9"),sQuery(id+"F0.wireOp",EDGE,"E6.5.1.10"),sQuery(id+"F0.wireOp",EDGE,"E6.5.1.11"),sQuery(id+"F0.wireOp",EDGE,"E6.5.2.0"),sQuery(id+"F0.wireOp",EDGE,"E6.5.2.1"),sQuery(id+"F0.wireOp",EDGE,"E6.5.2.2"),sQuery(id+"F0.wireOp",EDGE,"E6.5.2.3"),sQuery(id+"F0.wireOp",EDGE,"E6.5.2.4"),sQuery(id+"F0.wireOp",EDGE,"E6.5.2.5"),sQuery(id+"F0.wireOp",EDGE,"E6.5.2.6"),sQuery(id+"F0.wireOp",EDGE,"E6.5.2.7"),sQuery(id+"F0.wireOp",EDGE,"E6.5.2.8"),sQuery(id+"F0.wireOp",EDGE,"E6.5.2.9"),sQuery(id+"F0.wireOp",EDGE,"E6.5.2.10"),sQuery(id+"F0.wireOp",EDGE,"E6.5.2.11"),sQuery(id+"F0.wireOp",EDGE,"E6.5.3.0"),sQuery(id+"F0.wireOp",EDGE,"E6.5.3.1"),sQuery(id+"F0.wireOp",EDGE,"E6.5.3.2"),sQuery(id+"F0.wireOp",EDGE,"E6.6.0.0"),sQuery(id+"F0.wireOp",EDGE,"E6.6.0.1"),sQuery(id+"F0.wireOp",EDGE,"E6.6.0.2"),sQuery(id+"F0.wireOp",EDGE,"E6.6.0.3"),sQuery(id+"F0.wireOp",EDGE,"E6.6.0.4"),sQuery(id+"F0.wireOp",EDGE,"E6.6.0.5"),sQuery(id+"F0.wireOp",EDGE,"E6.6.0.6"),sQuery(id+"F0.wireOp",EDGE,"E6.6.0.7"),sQuery(id+"F0.wireOp",EDGE,"E6.6.0.8"),sQuery(id+"F0.wireOp",EDGE,"E6.6.0.9"),sQuery(id+"F0.wireOp",EDGE,"E6.6.0.10"),sQuery(id+"F0.wireOp",EDGE,"E6.6.0.11"),sQuery(id+"F0.wireOp",EDGE,"E6.6.1.0"),sQuery(id+"F0.wireOp",EDGE,"E6.6.1.1"),sQuery(id+"F0.wireOp",EDGE,"E6.6.1.2"),sQuery(id+"F0.wireOp",EDGE,"E6.6.1.3"),sQuery(id+"F0.wireOp",EDGE,"E6.6.1.4"),sQuery(id+"F0.wireOp",EDGE,"E6.6.1.5"),sQuery(id+"F0.wireOp",EDGE,"E6.6.1.6"),sQuery(id+"F0.wireOp",EDGE,"E6.6.1.7"),sQuery(id+"F0.wireOp",EDGE,"E6.6.1.8"),sQuery(id+"F0.wireOp",EDGE,"E6.6.1.9"),sQuery(id+"F0.wireOp",EDGE,"E6.6.1.10"),sQuery(id+"F0.wireOp",EDGE,"E6.6.1.11"),sQuery(id+"F0.wireOp",EDGE,"E6.6.2.0"),sQuery(id+"F0.wireOp",EDGE,"E6.6.2.1"),sQuery(id+"F0.wireOp",EDGE,"E6.6.2.2"),sQuery(id+"F0.wireOp",EDGE,"E6.6.2.3"),sQuery(id+"F0.wireOp",EDGE,"E6.6.2.4"),sQuery(id+"F0.wireOp",EDGE,"E6.6.2.5"),sQuery(id+"F0.wireOp",EDGE,"E6.6.2.6"),sQuery(id+"F0.wireOp",EDGE,"E6.6.2.7"),sQuery(id+"F0.wireOp",EDGE,"E6.6.2.8"),sQuery(id+"F0.wireOp",EDGE,"E6.6.2.9"),sQuery(id+"F0.wireOp",EDGE,"E6.6.2.10"),sQuery(id+"F0.wireOp",EDGE,"E6.6.2.11"),sQuery(id+"F0.wireOp",EDGE,"E6.6.3.0"),sQuery(id+"F0.wireOp",EDGE,"E6.6.3.1"),sQuery(id+"F0.wireOp",EDGE,"E6.6.3.2"),sQuery(id+"F0.wireOp",EDGE,"E6.6.3.5"),sQuery(id+"F0.wireOp",EDGE,"E6.7.0.0"),sQuery(id+"F0.wireOp",EDGE,"E6.7.0.1"),sQuery(id+"F0.wireOp",EDGE,"E6.7.0.2"),sQuery(id+"F0.wireOp",EDGE,"E6.7.0.3"),sQuery(id+"F0.wireOp",EDGE,"E6.7.0.4"),sQuery(id+"F0.wireOp",EDGE,"E6.7.0.5"),sQuery(id+"F0.wireOp",EDGE,"E6.7.0.6"),sQuery(id+"F0.wireOp",EDGE,"E6.7.0.7"),sQuery(id+"F0.wireOp",EDGE,"E6.7.0.8"),sQuery(id+"F0.wireOp",EDGE,"E6.7.0.9"),sQuery(id+"F0.wireOp",EDGE,"E6.7.0.10"),sQuery(id+"F0.wireOp",EDGE,"E6.7.0.11"),sQuery(id+"F0.wireOp",EDGE,"E6.7.1.0"),sQuery(id+"F0.wireOp",EDGE,"E6.7.1.1"),sQuery(id+"F0.wireOp",EDGE,"E6.7.1.2"),sQuery(id+"F0.wireOp",EDGE,"E6.7.1.3"),sQuery(id+"F0.wireOp",EDGE,"E6.7.1.4"),sQuery(id+"F0.wireOp",EDGE,"E6.7.1.5"),sQuery(id+"F0.wireOp",EDGE,"E6.7.1.6"),sQuery(id+"F0.wireOp",EDGE,"E6.7.1.7"),sQuery(id+"F0.wireOp",EDGE,"E6.7.1.8"),sQuery(id+"F0.wireOp",EDGE,"E6.7.1.9"),sQuery(id+"F0.wireOp",EDGE,"E6.7.1.10"),sQuery(id+"F0.wireOp",EDGE,"E6.7.1.11"),sQuery(id+"F0.wireOp",EDGE,"E6.7.2.0"),sQuery(id+"F0.wireOp",EDGE,"E6.7.2.1"),sQuery(id+"F0.wireOp",EDGE,"E6.7.2.2"),sQuery(id+"F0.wireOp",EDGE,"E6.7.2.3"),sQuery(id+"F0.wireOp",EDGE,"E6.7.2.4"),sQuery(id+"F0.wireOp",EDGE,"E6.7.2.5"),sQuery(id+"F0.wireOp",EDGE,"E6.7.2.6"),sQuery(id+"F0.wireOp",EDGE,"E6.7.2.7"),sQuery(id+"F0.wireOp",EDGE,"E6.7.2.8"),sQuery(id+"F0.wireOp",EDGE,"E6.7.2.9"),sQuery(id+"F0.wireOp",EDGE,"E6.7.2.10"),sQuery(id+"F0.wireOp",EDGE,"E6.7.2.11"),sQuery(id+"F0.wireOp",EDGE,"E6.7.3.0"),sQuery(id+"F0.wireOp",EDGE,"E6.7.3.1"),sQuery(id+"F0.wireOp",EDGE,"E6.7.3.2"),sQuery(id+"F0.wireOp",EDGE,"E6.7.3.5"),sQuery(id+"F0.wireOp",EDGE,"E6.8.0.0"),sQuery(id+"F0.wireOp",EDGE,"E6.8.0.2"),sQuery(id+"F0.wireOp",EDGE,"E6.8.0.3"),sQuery(id+"F0.wireOp",EDGE,"E6.8.0.4"),sQuery(id+"F0.wireOp",EDGE,"E6.8.0.5"),sQuery(id+"F0.wireOp",EDGE,"E6.8.0.6"),sQuery(id+"F0.wireOp",EDGE,"E6.8.0.7"),sQuery(id+"F0.wireOp",EDGE,"E6.8.0.8"),sQuery(id+"F0.wireOp",EDGE,"E6.8.0.9"),sQuery(id+"F0.wireOp",EDGE,"E6.8.0.10"),sQuery(id+"F0.wireOp",EDGE,"E6.8.0.11"),sQuery(id+"F0.wireOp",EDGE,"E6.8.1.0"),sQuery(id+"F0.wireOp",EDGE,"E6.8.1.1"),sQuery(id+"F0.wireOp",EDGE,"E6.8.1.2"),sQuery(id+"F0.wireOp",EDGE,"E6.8.1.3"),sQuery(id+"F0.wireOp",EDGE,"E6.8.1.4"),sQuery(id+"F0.wireOp",EDGE,"E6.8.1.5"),sQuery(id+"F0.wireOp",EDGE,"E6.8.1.6"),sQuery(id+"F0.wireOp",EDGE,"E6.8.1.7"),sQuery(id+"F0.wireOp",EDGE,"E6.8.1.8"),sQuery(id+"F0.wireOp",EDGE,"E6.8.1.9"),sQuery(id+"F0.wireOp",EDGE,"E6.8.1.10"),sQuery(id+"F0.wireOp",EDGE,"E6.8.1.11"),sQuery(id+"F0.wireOp",EDGE,"E6.8.2.0"),sQuery(id+"F0.wireOp",EDGE,"E6.8.2.1"),sQuery(id+"F0.wireOp",EDGE,"E6.8.2.2"),sQuery(id+"F0.wireOp",EDGE,"E6.8.2.3"),sQuery(id+"F0.wireOp",EDGE,"E6.8.2.4"),sQuery(id+"F0.wireOp",EDGE,"E6.8.2.5"),sQuery(id+"F0.wireOp",EDGE,"E6.8.2.6"),sQuery(id+"F0.wireOp",EDGE,"E6.8.2.7"),sQuery(id+"F0.wireOp",EDGE,"E6.8.2.8"),sQuery(id+"F0.wireOp",EDGE,"E6.8.2.9"),sQuery(id+"F0.wireOp",EDGE,"E6.8.2.10"),sQuery(id+"F0.wireOp",EDGE,"E6.8.2.11"),sQuery(id+"F0.wireOp",EDGE,"E6.8.3.0"),sQuery(id+"F0.wireOp",EDGE,"E6.8.3.1"),sQuery(id+"F0.wireOp",EDGE,"E6.9.0.6"),sQuery(id+"F0.wireOp",EDGE,"E6.9.0.7"),sQuery(id+"F0.wireOp",EDGE,"E6.9.0.8"),sQuery(id+"F0.wireOp",EDGE,"E6.9.0.9"),sQuery(id+"F0.wireOp",EDGE,"E6.9.0.10"),sQuery(id+"F0.wireOp",EDGE,"E6.9.0.11"),sQuery(id+"F0.wireOp",EDGE,"E6.9.1.0"),sQuery(id+"F0.wireOp",EDGE,"E6.9.1.1"),sQuery(id+"F0.wireOp",EDGE,"E6.9.1.2"),sQuery(id+"F0.wireOp",EDGE,"E6.9.1.3"),sQuery(id+"F0.wireOp",EDGE,"E6.9.1.4"),sQuery(id+"F0.wireOp",EDGE,"E6.9.1.5"),sQuery(id+"F0.wireOp",EDGE,"E6.9.1.6"),sQuery(id+"F0.wireOp",EDGE,"E6.9.1.7"),sQuery(id+"F0.wireOp",EDGE,"E6.9.1.8"),sQuery(id+"F0.wireOp",EDGE,"E6.9.1.9"),sQuery(id+"F0.wireOp",EDGE,"E6.9.1.10"),sQuery(id+"F0.wireOp",EDGE,"E6.9.1.11"),sQuery(id+"F0.wireOp",EDGE,"E6.9.2.0"),sQuery(id+"F0.wireOp",EDGE,"E6.9.2.1"),sQuery(id+"F0.wireOp",EDGE,"E6.9.2.2"),sQuery(id+"F0.wireOp",EDGE,"E6.9.2.3"),sQuery(id+"F0.wireOp",EDGE,"E6.9.2.4"),sQuery(id+"F0.wireOp",EDGE,"E6.9.2.5"),sQuery(id+"F0.wireOp",EDGE,"E6.9.2.6"),sQuery(id+"F0.wireOp",EDGE,"E6.9.2.7"),sQuery(id+"F0.wireOp",EDGE,"E6.9.2.8"),sQuery(id+"F0.wireOp",EDGE,"E6.9.2.10"),sQuery(id+"F0.wireOp",EDGE,"E6.9.2.11"),sQuery(id+"F0.wireOp",EDGE,"E6.10.0.6"),sQuery(id+"F0.wireOp",EDGE,"E6.10.0.10"),sQuery(id+"F0.wireOp",EDGE,"E6.10.0.11"),sQuery(id+"F0.wireOp",EDGE,"E6.10.1.0"),sQuery(id+"F0.wireOp",EDGE,"E6.10.1.4"),sQuery(id+"F0.wireOp",EDGE,"E6.10.1.5"),sQuery(id+"F0.wireOp",EDGE,"E6.10.1.6"),sQuery(id+"F0.wireOp",EDGE,"E6.10.1.7"),sQuery(id+"F0.wireOp",EDGE,"E6.10.1.9"),sQuery(id+"F0.wireOp",EDGE,"E6.10.1.10"),sQuery(id+"F0.wireOp",EDGE,"E6.10.1.11"),sQuery(id+"F0.wireOp",EDGE,"E6.10.2.0"),sQuery(id+"F0.wireOp",EDGE,"E6.10.2.5"),sQuery(id+"F0.wireOp",EDGE,"E7.trimOffspring"),sQuery(id+"F0.wireOp",EDGE,"E9"),sQuery(id+"F0.wireOp",EDGE,"E12.trimOffspring"),sQuery(id+"F0.wireOp",EDGE,"E13"),sQuery(id+"F0.wireOp",EDGE,"E14.trimOffspring"),sQuery(id+"F0.wireOp",EDGE,"E17"),sQuery(id+"F0.wireOp",EDGE,"E18.trimOffspring"),sQuery(id+"F0.wireOp",EDGE,"E26.trimOffspring"),sQuery(id+"F0.wireOp",EDGE,"E27.trimOffspring"),sQuery(id+"F0.wireOp",EDGE,"E28.trimOffspring"),sQuery(id+"F0.wireOp",EDGE,"E34"),sQuery(id+"F0.wireOp",EDGE,"E35"),sQuery(id+"F0.wireOp",EDGE,"E36"),sQuery(id+"F0.wireOp",EDGE,"E37"),sQuery(id+"F0.wireOp",EDGE,"E38"),sQuery(id+"F0.wireOp",EDGE,"E39"),sQuery(id+"F0.wireOp",EDGE,"E40"),sQuery(id+"F0.wireOp",EDGE,"E41"),sQuery(id+"F0.wireOp",EDGE,"E42"),sQuery(id+"F0.wireOp",EDGE,"E43"),sQuery(id+"F0.wireOp",EDGE,"E44"),sQuery(id+"F0.wireOp",EDGE,"E45"),sQuery(id+"F0.wireOp",EDGE,"E46"),sQuery(id+"F0.wireOp",EDGE,"E47"),sQuery(id+"F0.wireOp",EDGE,"E48"),sQuery(id+"F0.wireOp",EDGE,"E49")])],"isStart":false});
            cPlane(context, id + "F5", {"entities" : qUnion([Q0]), "cplaneType" : CPlaneType.OFFSET, "offset" : 0 * mm, "width" : 150 * mm, "height" : 150 * mm});
        }
        {
            var Q0;
            Q0=qCreatedBy(id+"F5.planeOp",FACE);
            var sketch = newSketch(context, id + "F6", { "sketchPlane" : qUnion([Q0])});
            skEllipse(sketch, "E50.0", {"center": v(0, 0) * mm, "majorRadius": 50 * mm, "minorRadius": 37.5 * mm, "majorAxis": v(-1, 0)});
            skFitSpline(sketch, "E51", {"points": [v(-9.88, 20.79) * mm, v(-12.62, 23.92) * mm, v(-13.8, 28.03) * mm, v(-14.77, 25.48) * mm, v(-17.41, 24.9) * mm, v(-9.88, 20.79) * mm]});
            skFitSpline(sketch, "E52", {"points": [v(-10.96, 19.32) * mm, v(-14.97, 20.79) * mm, v(-18.2, 23.43) * mm, v(-18.98, 26.66) * mm, v(-23.67, 22.45) * mm, v(-20.74, 19.42) * mm, v(-18.1, 16.58) * mm, v(-10.96, 19.32) * mm]});
            skFitSpline(sketch, "E53", {"points": [v(-16.83, 27.34) * mm, v(-17.51, 28.52) * mm, v(-19.37, 28.71) * mm, v(-13.4, 31.16) * mm, v(-14.97, 28.71) * mm, v(-15.26, 27.64) * mm, v(-16.83, 27.34) * mm]});
            skFitSpline(sketch, "E54", {"points": [v(-19.66, 15.5) * mm, v(-21.72, 18.05) * mm, v(-25.04, 20.7) * mm, v(-26.41, 16.68) * mm, v(-23.09, 13.94) * mm, v(-19.66, 15.5) * mm]});
            skFitSpline(sketch, "E55", {"points": [v(-21.33, 27.15) * mm, v(-25.04, 23.33) * mm, v(-27.3, 25.1) * mm, v(-21.33, 27.15) * mm]});
            skFitSpline(sketch, "E56", {"points": [v(-27, 20.98) * mm, v(-29.64, 23.43) * mm, v(-34.73, 20) * mm, v(-32.28, 17.56) * mm, v(-29.25, 16.88) * mm, v(-28.96, 18.93) * mm, v(-27, 20.98) * mm]});
            skFitSpline(sketch, "E57", {"points": [v(-24.85, 12.86) * mm, v(-27, 14.14) * mm, v(-27.79, 16.68) * mm, v(-28.93, 15.44) * mm, v(-32.14, 15.75) * mm, v(-30.12, 11.81) * mm, v(-24.85, 12.86) * mm]});
            skFitSpline(sketch, "E58", {"points": [v(-33.38, 16.58) * mm, v(-37.06, 18.34) * mm, v(-40.02, 14.5) * mm, v(-36.6, 11.71) * mm, v(-33.38, 16.58) * mm]});
            skFitSpline(sketch, "E59", {"points": [v(-33.02, 13.52) * mm, v(-33.75, 11.76) * mm, v(-36.44, 10) * mm, v(-31.36, 7.4) * mm, v(-28.36, 10.05) * mm, v(-31.83, 10.57) * mm, v(-33.02, 13.52) * mm]});
            skFitSpline(sketch, "E60", {"points": [v(-41.26, 12.85) * mm, v(-40.95, 10.1) * mm, v(-38.3, 9.12) * mm, v(-37.9, 7.25) * mm, v(-39.3, 5.75) * mm, v(-42.3, 4.87) * mm, v(-44.73, 7.77) * mm, v(-42.5, 13.16) * mm, v(-41.26, 12.85) * mm]});
            skFitSpline(sketch, "E61", {"points": [v(-35.98, 6.63) * mm, v(-37.01, 4.2) * mm, v(-40.64, 2.85) * mm, v(-36.13, -0.47) * mm, v(-31.78, 4.92) * mm, v(-35.98, 6.63) * mm]});
            skFitSpline(sketch, "E62", {"points": [v(-41.94, 3.32) * mm, v(-43.44, 2.49) * mm, v(-45.61, 3.89) * mm, v(-45.15, -2.07) * mm, v(-42.97, -1.66) * mm, v(-39.97, -1.5) * mm, v(-41.88, 0.83) * mm, v(-41.94, 3.32) * mm]});
            skFitSpline(sketch, "E63", {"points": [v(-44.32, -4.4) * mm, v(-42.25, -3.63) * mm, v(-39.08, -3.42) * mm, v(-40.07, -7.93) * mm, v(-44.32, -4.4) * mm]});
            skFitSpline(sketch, "E64", {"points": [v(-30.8, 1.2) * mm, v(-33.33, -2.02) * mm, v(-37.01, -2.18) * mm, v(-36.8, -5.18) * mm, v(-38.1, -8.09) * mm, v(-35.25, -9.07) * mm, v(-29.14, 1.3) * mm, v(-30.8, 1.2) * mm]});
            skFitSpline(sketch, "E65", {"points": [v(-30.12, 3.68) * mm, v(-30.8, 6.01) * mm, v(-28.77, 6.06) * mm, v(-27.01, 9.17) * mm, v(-22.92, 7.25) * mm, v(-27.43, 1.2) * mm, v(-28.2, 2.6) * mm, v(-30.12, 3.68) * mm]});
            skFitSpline(sketch, "E66", {"points": [v(-22.77, 11.12) * mm, v(-20.07, 10.07) * mm, v(-20.33, 5.89) * mm, v(-13.19, 9.2) * mm, v(-16.32, 13.56) * mm, v(-22.25, 12.77) * mm, v(-22.77, 11.12) * mm]});
            skFitSpline(sketch, "E67", {"points": [v(-14.4, 15.13) * mm, v(-10.13, 16.35) * mm, v(-9, 18) * mm, v(-7.26, 16) * mm, v(-11.53, 11.47) * mm, v(-12.23, 13.3) * mm, v(-14.4, 15.13) * mm]});
            skFitSpline(sketch, "E68", {"points": [v(0, 31.51) * mm, v(3.03, 20.96) * mm, v(-1.94, 1.62) * mm, v(0, -17.03) * mm, v(-2.45, -30.26) * mm], "startDerivative": vector(23.64, -46.23) * mm, "endDerivative": vector(-17.09, -54.55) * mm, "construction": true});
            skFitSpline(sketch, "E69", {"points": [v(-2.43, 31.72) * mm, v(0, 27.04) * mm, v(-0.87, 25.3) * mm, v(-4.65, 25.64) * mm, v(-6.8, 28.68) * mm, v(-2.43, 31.72) * mm]});
            skFitSpline(sketch, "E70", {"points": [v(-6.8, 25.3) * mm, v(-4.65, 23.83) * mm, v(-0.7, 23) * mm, v(1.1, 24.32) * mm, v(1.43, 22.51) * mm, v(0, 19.14) * mm, v(-5.72, 18.73) * mm, v(-8.2, 23.58) * mm, v(-6.8, 25.3) * mm]});
            skFitSpline(sketch, "E71", {"points": [v(0, 17.33) * mm, v(-5.56, 16.34) * mm, v(-6.3, 11.74) * mm, v(-3.34, 9.68) * mm, v(0, 13.7) * mm, v(0, 17.33) * mm]});
            skFitSpline(sketch, "E72", {"points": [v(-3.34, 7.62) * mm, v(-6.8, 7.87) * mm, v(-9.1, 9.68) * mm, v(-11.65, 7.87) * mm, v(-6.63, 3.5) * mm, v(-3.34, 4.17) * mm, v(-3.34, 7.62) * mm]});
            skFitSpline(sketch, "E73", {"points": [v(-4.73, 1.17) * mm, v(-6.8, 1.72) * mm, v(-7.7, -1.36) * mm, v(-6.8, -2.34) * mm, v(-4.73, -3.77) * mm, v(-3.34, -0.92) * mm, v(-4.62, 0) * mm, v(-4.73, 1.17) * mm]});
            skFitSpline(sketch, "E74", {"points": [v(-9.12, 2.3) * mm, v(-9.85, 0) * mm, v(-9.38, -2) * mm, v(-8.5, -3.14) * mm, v(-14.61, -4.38) * mm, v(-16.69, 0) * mm, v(-11.56, 3.03) * mm, v(-9.12, 2.3) * mm]});
            skFitSpline(sketch, "E75", {"points": [v(-18.5, 2.61) * mm, v(-19.7, 0) * mm, v(-18.7, -2.41) * mm, v(-16.95, -6.1) * mm, v(-20.78, -7.13) * mm, v(-25.08, -1.17) * mm, v(-21.66, 3.5) * mm, v(-18.5, 2.61) * mm]});
            skFitSpline(sketch, "E76", {"points": [v(-3.27, -5.73) * mm, v(-3, -8.68) * mm, v(-4.82, -11.53) * mm, v(-8.45, -10.34) * mm, v(-9.38, -5.37) * mm, v(-7.83, -5.47) * mm, v(-4.82, -5.1) * mm, v(-3.27, -5.73) * mm]});
            skFitSpline(sketch, "E77", {"points": [v(-11.76, -6.14) * mm, v(-13.32, -6.45) * mm, v(-14.87, -6.2) * mm, v(-14.72, -7.7) * mm, v(-16.53, -8.73) * mm, v(-14.4, -12.26) * mm, v(-12.28, -11.8) * mm, v(-10.1, -11.84) * mm, v(-11.92, -9.56) * mm, v(-11.76, -6.14) * mm]});
            skFitSpline(sketch, "E78", {"points": [v(-19.9, -9.62) * mm, v(-22.85, -9.51) * mm, v(-25.34, -6.5) * mm, v(-27.2, -3.6) * mm, v(-29.28, -4.85) * mm, v(-29.7, -6.92) * mm, v(-32.9, -10.24) * mm, v(-31.56, -13.14) * mm, v(-18.97, -12.41) * mm, v(-19.07, -10.96) * mm, v(-19.9, -9.62) * mm]});
            skFitSpline(sketch, "E79", {"points": [v(-2.31, -12.56) * mm, v(-2.22, -14.56) * mm, v(-2.57, -16.57) * mm, v(-5.1, -16.4) * mm, v(-7.37, -13.26) * mm, v(-4.5, -13.6) * mm, v(-2.31, -12.56) * mm]});
            skFitSpline(sketch, "E80", {"points": [v(-8.33, -16.66) * mm, v(-9.72, -14.22) * mm, v(-14.51, -14.56) * mm, v(-13.82, -17) * mm, v(-13.82, -18.83) * mm, v(-9.37, -19.27) * mm, v(-8.33, -16.66) * mm]});
            skFitSpline(sketch, "E81", {"points": [v(-2.31, -18.83) * mm, v(-3.36, -19.53) * mm, v(-5.71, -18.31) * mm, v(-6.15, -20.06) * mm, v(-7.54, -21.01) * mm, v(-5.19, -23.28) * mm, v(-3, -23.45) * mm, v(-2.31, -18.83) * mm]});
            skFitSpline(sketch, "E82", {"points": [v(-19.13, -14.13) * mm, v(-16.6, -15.61) * mm, v(-16.08, -17.35) * mm, v(-16.6, -18.75) * mm, v(-20, -18.75) * mm, v(-23.49, -15.26) * mm, v(-21.4, -14.4) * mm, v(-19.13, -14.13) * mm]});
            skFitSpline(sketch, "E83", {"points": [v(-25.76, -15.35) * mm, v(-31.07, -14.83) * mm, v(-33.51, -13.95) * mm, v(-33.95, -16.4) * mm, v(-30.9, -18.83) * mm, v(-27.15, -21.36) * mm, v(-25.93, -21.19) * mm, v(-23.93, -18.05) * mm, v(-24.01, -16.48) * mm, v(-25.76, -15.35) * mm]});
            skFitSpline(sketch, "E84", {"points": [v(-35.52, -11.34) * mm, v(-41, -10.56) * mm, v(-40.4, -14.13) * mm, v(-38.92, -15.17) * mm, v(-36.82, -15.7) * mm, v(-36.04, -14.56) * mm, v(-35.52, -11.34) * mm]});
            skFitSpline(sketch, "E85", {"points": [v(-34.9, -18.57) * mm, v(-28.54, -22.93) * mm, v(-28.37, -24.5) * mm, v(-28.1, -25.98) * mm, v(-35.52, -21.36) * mm, v(-35.52, -19.7) * mm, v(-34.9, -18.57) * mm]});
            skFitSpline(sketch, "E86", {"points": [v(-22.36, -18.57) * mm, v(-24.36, -21.71) * mm, v(-24.97, -24.76) * mm, v(-23.58, -26.77) * mm, v(-20.96, -25.72) * mm, v(-20, -25.11) * mm, v(-20.18, -20.67) * mm, v(-21.49, -20.23) * mm, v(-22.36, -18.57) * mm]});
            skFitSpline(sketch, "E87", {"points": [v(-16.43, -21.45) * mm, v(-13.47, -21.54) * mm, v(-11.11, -21.97) * mm, v(-12.33, -25.28) * mm, v(-15.3, -25.46) * mm, v(-16.52, -24.59) * mm, v(-16.43, -21.45) * mm]});
            skFitSpline(sketch, "E88", {"points": [v(-3.41, -25.46) * mm, v(-4.98, -25.46) * mm, v(-7.72, -24.12) * mm, v(-8.64, -27.78) * mm, v(-5.1, -29.08) * mm, v(-3.54, -28.17) * mm, v(-3.41, -25.46) * mm]});
            skFitSpline(sketch, "E89", {"points": [v(-20.67, -28.2) * mm, v(-18.4, -26.61) * mm, v(-16.04, -27.65) * mm, v(-11.89, -27.58) * mm, v(-11.33, -29.38) * mm, v(-13.69, -31.25) * mm, v(-17.35, -30.49) * mm, v(-20.67, -28.2) * mm]});
            skFitSpline(sketch, "E90", {"points": [v(-8.57, -30.07) * mm, v(-6.56, -30.9) * mm, v(-4.21, -30.42) * mm, v(-4.28, -32.15) * mm, v(-5.18, -33.04) * mm, v(-9.95, -32.5) * mm, v(-10.3, -30.83) * mm, v(-8.57, -30.07) * mm]});
            skFitSpline(sketch, "E91", {"points": [v(3.5, 31.76) * mm, v(7.09, 30.93) * mm, v(8.75, 28.28) * mm, v(7.5, 25.54) * mm, v(5.01, 24.98) * mm, v(4.32, 28.28) * mm, v(3.5, 31.76) * mm]});
            skFitSpline(sketch, "E92", {"points": [v(5.15, 22.5) * mm, v(5.84, 19.31) * mm, v(4.18, 16.96) * mm, v(5.84, 15.58) * mm, v(10.4, 20.83) * mm, v(8.33, 23.19) * mm, v(5.15, 22.5) * mm]});
            skFitSpline(sketch, "E93", {"points": [v(4.6, 13.78) * mm, v(2.8, 10.6) * mm, v(4.04, 9.07) * mm, v(7.78, 10.32) * mm, v(8.33, 12.4) * mm, v(4.6, 13.78) * mm]});
            skFitSpline(sketch, "E94", {"points": [v(2.1, 7.7) * mm, v(4.04, 5.48) * mm, v(6.81, 6.86) * mm, v(9.44, 7.14) * mm, v(8.89, 4.92) * mm, v(7.5, 1.74) * mm, v(1.7, 2.3) * mm, v(1, 5.2) * mm, v(2.1, 7.7) * mm]});
            skFitSpline(sketch, "E95", {"points": [v(7.23, -1.16) * mm, v(3.21, -1.58) * mm, v(0, -3.8) * mm, v(0, -5.73) * mm, v(4.18, -6.97) * mm, v(7.64, -6.84) * mm, v(7.23, -1.16) * mm]});
            skFitSpline(sketch, "E96", {"points": [v(9.16, -9.88) * mm, v(6.12, -10.57) * mm, v(1.7, -9.19) * mm, v(2.1, -15.41) * mm, v(6.81, -16.1) * mm, v(9.44, -16.1) * mm, v(10.55, -13.34) * mm, v(9.16, -9.88) * mm]});
            skFitSpline(sketch, "E97", {"points": [v(9.44, -18.73) * mm, v(2.66, -18.73) * mm, v(2.1, -19.7) * mm, v(2.25, -22.05) * mm, v(1.97, -24.13) * mm, v(4.87, -24.13) * mm, v(6.95, -22.05) * mm, v(9.44, -18.73) * mm]});
            skFitSpline(sketch, "E98", {"points": [v(1.83, -26.48) * mm, v(5.84, -26.9) * mm, v(7.37, -30.08) * mm, v(5.43, -31.46) * mm, v(0, -31.6) * mm, v(1.83, -26.48) * mm]});
            skFitSpline(sketch, "E99", {"points": [v(10.69, 30.93) * mm, v(12.07, 28.86) * mm, v(10.55, 25.95) * mm, v(12.48, 23.46) * mm, v(17.6, 22.36) * mm, v(20.78, 26.92) * mm, v(17.88, 30.93) * mm, v(10.69, 30.93) * mm]});
            skFitSpline(sketch, "E100", {"points": [v(13.31, 20.14) * mm, v(10.96, 16.13) * mm, v(11.93, 12.4) * mm, v(16.5, 14.2) * mm, v(13.31, 20.14) * mm]});
            skFitSpline(sketch, "E101", {"points": [v(18.85, 19.45) * mm, v(20.78, 16.68) * mm, v(19.95, 12.67) * mm, v(24.1, 11.01) * mm, v(24.94, 23.19) * mm, v(23.14, 21.11) * mm, v(18.85, 19.45) * mm]});
            skFitSpline(sketch, "E102", {"points": [v(21.9, 7.83) * mm, v(18.7, 8.94) * mm, v(16.77, 10.32) * mm, v(13.45, 8.94) * mm, v(12.62, 5.75) * mm, v(17.88, 1.74) * mm, v(23.14, 2.85) * mm, v(21.9, 7.83) * mm]});
            skFitSpline(sketch, "E103", {"points": [v(21.61, -1.58) * mm, v(18.43, -1.86) * mm, v(14.42, 0) * mm, v(12.62, 1.88) * mm, v(10.55, 0) * mm, v(10.82, -3.65) * mm, v(10.82, -5.04) * mm, v(11.93, -7.11) * mm, v(16.91, -7.39) * mm, v(18.3, -6.42) * mm, v(21.9, -3.24) * mm, v(21.61, -1.58) * mm]});
            skFitSpline(sketch, "E104", {"points": [v(19.4, -8.91) * mm, v(16.63, -10.43) * mm, v(13.31, -9.74) * mm, v(14.42, -13.9) * mm, v(14.42, -16.1) * mm, v(16.63, -16.38) * mm, v(20.65, -12.23) * mm, v(19.4, -8.91) * mm]});
            skFitSpline(sketch, "E105", {"points": [v(16.08, -19.01) * mm, v(12.48, -17.9) * mm, v(12.2, -21.5) * mm, v(10.55, -24.27) * mm, v(15.39, -24.68) * mm, v(20.1, -19.29) * mm, v(16.08, -19.01) * mm]});
            skFitSpline(sketch, "E106", {"points": [v(15.39, -27.59) * mm, v(10.96, -27.59) * mm, v(12.2, -29.1) * mm, v(11.24, -31.19) * mm, v(20.5, -27.73) * mm, v(17.46, -26.2) * mm, v(15.39, -27.59) * mm]});
            skFitSpline(sketch, "E107", {"points": [v(20.78, -23.85) * mm, v(23.55, -21.36) * mm, v(24.8, -18.18) * mm, v(27.43, -19.56) * mm, v(27.15, -23.71) * mm, v(24.24, -26.2) * mm, v(20.78, -23.85) * mm]});
            skFitSpline(sketch, "E108", {"points": [v(24.52, -14.3) * mm, v(24.8, -11.12) * mm, v(22.58, -7.8) * mm, v(27.56, -6.56) * mm, v(31.02, -11.82) * mm, v(31.85, -16.52) * mm, v(29.09, -16.52) * mm, v(27.43, -14.86) * mm, v(24.52, -14.3) * mm]});
            skFitSpline(sketch, "E109", {"points": [v(26.87, -2.69) * mm, v(29.92, -2.69) * mm, v(31.44, -4.35) * mm, v(31.58, -6.7) * mm, v(32.96, -8.63) * mm, v(35.86, -6.84) * mm, v(34.07, 0) * mm, v(27.98, 2.3) * mm, v(26.87, -2.69) * mm]});
            skFitSpline(sketch, "E110", {"points": [v(35.73, -10.99) * mm, v(35.45, -13.9) * mm, v(34.34, -17.21) * mm, v(36.42, -18.18) * mm, v(40.7, -12.37) * mm, v(40.3, -10.7) * mm, v(35.73, -10.99) * mm]});
            skFitSpline(sketch, "E111", {"points": [v(33.86, -20.17) * mm, v(31.58, -19.32) * mm, v(30.27, -20.04) * mm, v(29.88, -22.46) * mm, v(29.5, -24.09) * mm, v(30.34, -25.33) * mm, v(33.93, -22.39) * mm, v(33.86, -20.17) * mm]});
            skFitSpline(sketch, "E112", {"points": [v(25.55, 7.07) * mm, v(26.38, 4.86) * mm, v(28.6, 5) * mm, v(32.4, 4.51) * mm, v(28.25, 11.98) * mm, v(25.55, 7.07) * mm]});
            skFitSpline(sketch, "E113", {"points": [v(36.48, 0) * mm, v(37.8, -3.3) * mm, v(37.66, -7.6) * mm, v(38.7, -8.42) * mm, v(41.67, -8.15) * mm, v(43.12, -8.9) * mm, v(44.37, 1.4) * mm, v(36.48, 0) * mm]});
            skFitSpline(sketch, "E114", {"points": [v(33.02, 11.84) * mm, v(34.54, 7.55) * mm, v(34.96, 5.13) * mm, v(36.07, 3.13) * mm, v(37.1, 3.82) * mm, v(43.74, 4.03) * mm, v(41.88, 10.6) * mm, v(40.22, 11.77) * mm, v(34.54, 12.4) * mm, v(33.02, 11.84) * mm]});
            skFitSpline(sketch, "E115", {"points": [v(27.98, 23.13) * mm, v(27.98, 20.83) * mm, v(26.95, 16.47) * mm, v(27.98, 14.25) * mm, v(30.65, 14.99) * mm, v(34.68, 14.99) * mm, v(32.54, 21.24) * mm, v(27.98, 23.13) * mm]});
            skFitSpline(sketch, "E116", {"points": [v(36.57, 19.1) * mm, v(37.07, 17.12) * mm, v(36.74, 14.99) * mm, v(37.64, 14.16) * mm, v(41.1, 13.5) * mm, v(39.78, 17.04) * mm, v(36.57, 19.1) * mm]});
            skFitSpline(sketch, "E117", {"points": [v(23.41, 28.07) * mm, v(23.74, 26.5) * mm, v(23, 25.02) * mm, v(24.56, 25.68) * mm, v(27.86, 25.19) * mm, v(29.09, 25.84) * mm, v(23.74, 28.97) * mm, v(23.41, 28.07) * mm]});
            skSolve(sketch);
        }
        {
            var Q0;
            Q0=makeQuery(id+"F6.imprint","IMPRINT",FACE,{"disambiguationData":[TD([[makeQuery(id+"F6.imprint","IMPRINT",EDGE,{"derivedFrom":sQuery(id+"F6.wireOp",EDGE,"E50.0")}),1.0]])]});
            extrude(context, id + "F7", {"entities" : qUnion([Q0]), "depth" : 1.5 * mm});
        }
    });
